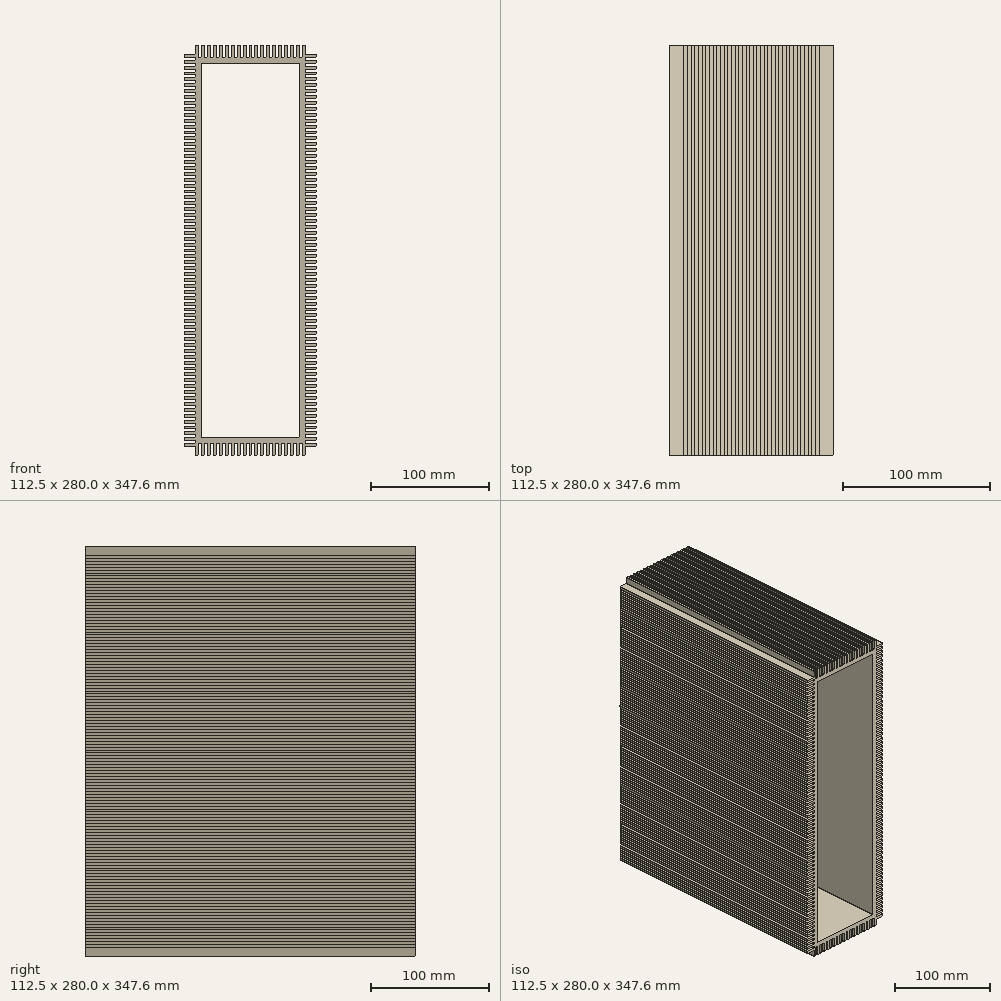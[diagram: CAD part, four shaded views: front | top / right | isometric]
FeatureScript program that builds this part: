
annotation { "Feature Type Name" : "Feature", "Feature Type Description" : "" }
export const myFeature = defineFeature(function(context is Context, id is Id, definition is map)
    precondition{}
    {
        {
            var Q0;
            Q0=qCreatedBy(makeId("Front.planeOp"),FACE);
            var sketch = newSketch(context, id + "F0", { "sketchPlane" : qUnion([Q0])});
            skLineSegment(sketch, "E0.bottom", {"start": v(40.56, -80) * mm, "end": v(-40.56, -80) * mm});
            skLineSegment(sketch, "E0.top", {"start": v(40.56, 80) * mm, "end": v(-40.56, 80) * mm});
            skLineSegment(sketch, "E0.left", {"start": v(40.56, -80) * mm, "end": v(40.56, 80) * mm});
            skLineSegment(sketch, "E0.right", {"start": v(-40.56, -80) * mm, "end": v(-40.56, 80) * mm});
            skPoint(sketch, "E0.middle", {"position": v(0, 0) * mm});
            skLineSegment(sketch, "E1", {"start": v(40.56, 80) * mm, "end": v(40.56, 85) * mm});
            skLineSegment(sketch, "E2", {"start": v(40.56, 85) * mm, "end": v(45.56, 85) * mm});
            skLineSegment(sketch, "E3.bottom", {"start": v(45.56, 85) * mm, "end": v(-45.56, 85) * mm});
            skLineSegment(sketch, "E3.left", {"start": v(45.56, 85) * mm, "end": v(45.56, -80) * mm});
            skLineSegment(sketch, "E3.right", {"start": v(-45.56, 85) * mm, "end": v(-45.56, -80) * mm});
            skLineSegment(sketch, "E4", {"start": v(-45.56, -80) * mm, "end": v(45.56, -80) * mm});
            skSolve(sketch);
        }
        {
            var Q0;
            Q0=makeQuery(id+"F0.imprint","IMPRINT",FACE,{"disambiguationData":[TD([[makeQuery(id+"F0.imprint","IMPRINT",EDGE,{"derivedFrom":sQuery(id+"F0.wireOp",EDGE,"E0.top")}),-1.0]])]});
            var Q1;
            {var subQ3=sQuery(id+"F0.wireOp",EDGE,"E0.left");Q1=makeQuery(id+"F0.imprint","IMPRINT",FACE,{"disambiguationData":[TD([[makeQuery(id+"F0.imprint","IMPRINT",EDGE,{"derivedFrom":subQ3}),-1.0]])]});}
            extrude(context, id + "F1", {"entities" : qUnion([Q0, Q1]), "depth" : 280 * mm, "offsetDistance" : 25 * mm});
        }
        {
            var Q0;
            Q0=makeQuery(id+"F1.opExtrude","SWEPT_FACE",FACE,{"disambiguationData":[OSD([sQuery(id+"F0.wireOp",EDGE,"E3.bottom")])]});
            extrude(context, id + "F2", {"entities" : qUnion([Q0]), "operationType" : NewBodyOperationType.ADD, "depth" : 0.05 * mm, "offsetDistance" : 25 * mm});
        }
        {
            var Q0;
            Q0=makeQuery(id+"F1.opExtrude","SWEPT_FACE",FACE,{"disambiguationData":[OSD([sQuery(id+"F0.wireOp",EDGE,"E0.top")])]});
            extrude(context, id + "F3", {"entities" : qUnion([Q0]), "operationType" : NewBodyOperationType.REMOVE, "oppositeDirection" : true, "depth" : 0.05 * mm, "offsetDistance" : 25 * mm});
        }
        {
            var Q0;
            {var subQ0=sQuery(id+"F0.wireOp",EDGE,"E3.left");Q0=makeQuery(id+"F2.boolean.opBoolean","MERGE",FACE,{"derivedFrom":[makeQuery(id+"F1.opExtrude","SWEPT_FACE",FACE,{"disambiguationData":[OSD([subQ0])]}),makeQuery(id+"F2.opExtrude","SWEPT_FACE",FACE,{"disambiguationData":[OSD([sQuery(id+"F0.wireOp",EDGE,"E3.bottom"),subQ0])]})]});}
            extrude(context, id + "F4", {"entities" : qUnion([Q0]), "operationType" : NewBodyOperationType.ADD, "depth" : 1.38 * mm, "offsetDistance" : 25 * mm});
        }
        {
            var Q0;
            {var subQ0=sQuery(id+"F0.wireOp",EDGE,"E0.left");Q0=makeQuery(id+"F3.boolean.opBoolean","MERGE",FACE,{"derivedFrom":[makeQuery(id+"F1.opExtrude","SWEPT_FACE",FACE,{"disambiguationData":[OSD([subQ0])]}),makeQuery(id+"F3.opExtrude","SWEPT_FACE",FACE,{"disambiguationData":[OSD([sQuery(id+"F0.wireOp",EDGE,"E0.top"),subQ0,sQuery(id+"F0.wireOp",EDGE,"E1")])]})]});}
            extrude(context, id + "F5", {"entities" : qUnion([Q0]), "operationType" : NewBodyOperationType.REMOVE, "oppositeDirection" : true, "depth" : 1.38 * mm, "offsetDistance" : 25 * mm});
        }
        {
            var Q0;
            Q0=makeQuery(id+"F1.opExtrude","CAP_FACE",FACE,{"disambiguationData":[OSD([sQuery(id+"F0.wireOp",EDGE,"E0.top"),sQuery(id+"F0.wireOp",EDGE,"E0.left"),sQuery(id+"F0.wireOp",EDGE,"E0.right"),sQuery(id+"F0.wireOp",EDGE,"E3.bottom"),sQuery(id+"F0.wireOp",EDGE,"E3.left"),sQuery(id+"F0.wireOp",EDGE,"E3.right"),sQuery(id+"F0.wireOp",EDGE,"E4")])],"isStart":false});
            var sketch = newSketch(context, id + "F6", { "sketchPlane" : qUnion([Q0])});
            skLineSegment(sketch, "E5.bottom", {"start": v(-45.56, -80) * mm, "end": v(-55.56, -80) * mm});
            skLineSegment(sketch, "E5.top", {"start": v(-45.56, -77.5) * mm, "end": v(-55.56, -77.5) * mm});
            skLineSegment(sketch, "E5.left", {"start": v(-45.56, -80) * mm, "end": v(-45.56, -77.5) * mm});
            skLineSegment(sketch, "E5.right", {"start": v(-55.56, -80) * mm, "end": v(-55.56, -77.5) * mm});
            skLineSegment(sketch, "E6", {"start": v(-45.56, -77.5) * mm, "end": v(-45.56, -75) * mm});
            skLineSegment(sketch, "E7.bottom", {"start": v(-45.56, -75) * mm, "end": v(-55.56, -75) * mm});
            skLineSegment(sketch, "E7.top", {"start": v(-45.56, -72.5) * mm, "end": v(-55.56, -72.5) * mm});
            skLineSegment(sketch, "E7.left", {"start": v(-45.56, -75) * mm, "end": v(-45.56, -72.5) * mm});
            skLineSegment(sketch, "E7.right", {"start": v(-55.56, -75) * mm, "end": v(-55.56, -72.5) * mm});
            skLineSegment(sketch, "E8", {"start": v(-45.56, -72.5) * mm, "end": v(-45.56, -70) * mm});
            skLineSegment(sketch, "E9.bottom", {"start": v(-45.56, -70) * mm, "end": v(-55.56, -70) * mm});
            skLineSegment(sketch, "E9.top", {"start": v(-45.56, -67.5) * mm, "end": v(-55.56, -67.5) * mm});
            skLineSegment(sketch, "E9.left", {"start": v(-45.56, -70) * mm, "end": v(-45.56, -67.5) * mm});
            skLineSegment(sketch, "E9.right", {"start": v(-55.56, -70) * mm, "end": v(-55.56, -67.5) * mm});
            skLineSegment(sketch, "E10", {"start": v(-45.56, -67.5) * mm, "end": v(-45.56, -65) * mm});
            skLineSegment(sketch, "E11.bottom", {"start": v(-45.56, -65) * mm, "end": v(-55.56, -65) * mm});
            skLineSegment(sketch, "E11.top", {"start": v(-45.56, -62.5) * mm, "end": v(-55.56, -62.5) * mm});
            skLineSegment(sketch, "E11.left", {"start": v(-45.56, -65) * mm, "end": v(-45.56, -62.5) * mm});
            skLineSegment(sketch, "E11.right", {"start": v(-55.56, -65) * mm, "end": v(-55.56, -62.5) * mm});
            skLineSegment(sketch, "E12", {"start": v(-45.56, -62.5) * mm, "end": v(-45.56, -60) * mm});
            skLineSegment(sketch, "E13.bottom", {"start": v(-45.56, -60) * mm, "end": v(-55.56, -60) * mm});
            skLineSegment(sketch, "E13.top", {"start": v(-45.56, -57.5) * mm, "end": v(-55.56, -57.5) * mm});
            skLineSegment(sketch, "E13.left", {"start": v(-45.56, -60) * mm, "end": v(-45.56, -57.5) * mm});
            skLineSegment(sketch, "E13.right", {"start": v(-55.56, -60) * mm, "end": v(-55.56, -57.5) * mm});
            skLineSegment(sketch, "E14", {"start": v(-45.56, -57.5) * mm, "end": v(-45.56, -55) * mm});
            skLineSegment(sketch, "E15.bottom", {"start": v(-45.56, -55) * mm, "end": v(-55.56, -55) * mm});
            skLineSegment(sketch, "E15.top", {"start": v(-45.56, -52.5) * mm, "end": v(-55.56, -52.5) * mm});
            skLineSegment(sketch, "E15.left", {"start": v(-45.56, -55) * mm, "end": v(-45.56, -52.5) * mm});
            skLineSegment(sketch, "E15.right", {"start": v(-55.56, -55) * mm, "end": v(-55.56, -52.5) * mm});
            skLineSegment(sketch, "E16", {"start": v(-45.56, -52.5) * mm, "end": v(-45.56, -50) * mm});
            skLineSegment(sketch, "E17.bottom", {"start": v(-45.56, -50) * mm, "end": v(-55.56, -50) * mm});
            skLineSegment(sketch, "E17.top", {"start": v(-45.56, -47.5) * mm, "end": v(-55.56, -47.5) * mm});
            skLineSegment(sketch, "E17.left", {"start": v(-45.56, -50) * mm, "end": v(-45.56, -47.5) * mm});
            skLineSegment(sketch, "E17.right", {"start": v(-55.56, -50) * mm, "end": v(-55.56, -47.5) * mm});
            skLineSegment(sketch, "E18", {"start": v(-45.56, -47.5) * mm, "end": v(-45.56, -45) * mm});
            skLineSegment(sketch, "E19.bottom", {"start": v(-45.56, -45) * mm, "end": v(-55.56, -45) * mm});
            skLineSegment(sketch, "E19.top", {"start": v(-45.56, -42.5) * mm, "end": v(-55.56, -42.5) * mm});
            skLineSegment(sketch, "E19.left", {"start": v(-45.56, -45) * mm, "end": v(-45.56, -42.5) * mm});
            skLineSegment(sketch, "E19.right", {"start": v(-55.56, -45) * mm, "end": v(-55.56, -42.5) * mm});
            skLineSegment(sketch, "E20", {"start": v(-45.56, -42.5) * mm, "end": v(-45.56, -40) * mm});
            skLineSegment(sketch, "E21.bottom", {"start": v(-45.56, -40) * mm, "end": v(-55.56, -40) * mm});
            skLineSegment(sketch, "E21.top", {"start": v(-45.56, -37.5) * mm, "end": v(-55.56, -37.5) * mm});
            skLineSegment(sketch, "E21.left", {"start": v(-45.56, -40) * mm, "end": v(-45.56, -37.5) * mm});
            skLineSegment(sketch, "E21.right", {"start": v(-55.56, -40) * mm, "end": v(-55.56, -37.5) * mm});
            skLineSegment(sketch, "E22", {"start": v(-45.56, -37.5) * mm, "end": v(-45.56, -35) * mm});
            skLineSegment(sketch, "E23.bottom", {"start": v(-45.56, -35) * mm, "end": v(-55.56, -35) * mm});
            skLineSegment(sketch, "E23.top", {"start": v(-45.56, -32.5) * mm, "end": v(-55.56, -32.5) * mm});
            skLineSegment(sketch, "E23.left", {"start": v(-45.56, -35) * mm, "end": v(-45.56, -32.5) * mm});
            skLineSegment(sketch, "E23.right", {"start": v(-55.56, -35) * mm, "end": v(-55.56, -32.5) * mm});
            skLineSegment(sketch, "E24", {"start": v(-45.56, -32.5) * mm, "end": v(-45.56, -30) * mm});
            skLineSegment(sketch, "E25.bottom", {"start": v(-45.56, -30) * mm, "end": v(-55.56, -30) * mm});
            skLineSegment(sketch, "E25.top", {"start": v(-45.56, -27.5) * mm, "end": v(-55.56, -27.5) * mm});
            skLineSegment(sketch, "E25.left", {"start": v(-45.56, -30) * mm, "end": v(-45.56, -27.5) * mm});
            skLineSegment(sketch, "E25.right", {"start": v(-55.56, -30) * mm, "end": v(-55.56, -27.5) * mm});
            skLineSegment(sketch, "E26", {"start": v(-45.56, -27.5) * mm, "end": v(-45.56, -25) * mm});
            skLineSegment(sketch, "E27.bottom", {"start": v(-45.56, -25) * mm, "end": v(-55.56, -25) * mm});
            skLineSegment(sketch, "E27.top", {"start": v(-45.56, -22.5) * mm, "end": v(-55.56, -22.5) * mm});
            skLineSegment(sketch, "E27.left", {"start": v(-45.56, -25) * mm, "end": v(-45.56, -22.5) * mm});
            skLineSegment(sketch, "E27.right", {"start": v(-55.56, -25) * mm, "end": v(-55.56, -22.5) * mm});
            skLineSegment(sketch, "E28", {"start": v(-45.56, -22.5) * mm, "end": v(-45.56, -20) * mm});
            skLineSegment(sketch, "E29.bottom", {"start": v(-45.56, -20) * mm, "end": v(-55.56, -20) * mm});
            skLineSegment(sketch, "E29.top", {"start": v(-45.56, -17.5) * mm, "end": v(-55.56, -17.5) * mm});
            skLineSegment(sketch, "E29.left", {"start": v(-45.56, -20) * mm, "end": v(-45.56, -17.5) * mm});
            skLineSegment(sketch, "E29.right", {"start": v(-55.56, -20) * mm, "end": v(-55.56, -17.5) * mm});
            skLineSegment(sketch, "E30", {"start": v(-45.56, -17.5) * mm, "end": v(-45.56, -15) * mm});
            skLineSegment(sketch, "E31.bottom", {"start": v(-45.56, -15) * mm, "end": v(-55.56, -15) * mm});
            skLineSegment(sketch, "E31.top", {"start": v(-45.56, -12.5) * mm, "end": v(-55.56, -12.5) * mm});
            skLineSegment(sketch, "E31.left", {"start": v(-45.56, -15) * mm, "end": v(-45.56, -12.5) * mm});
            skLineSegment(sketch, "E31.right", {"start": v(-55.56, -15) * mm, "end": v(-55.56, -12.5) * mm});
            skLineSegment(sketch, "E32", {"start": v(-45.56, -12.5) * mm, "end": v(-45.56, -10) * mm});
            skLineSegment(sketch, "E33.bottom", {"start": v(-45.56, -10) * mm, "end": v(-55.56, -10) * mm});
            skLineSegment(sketch, "E33.top", {"start": v(-45.56, -7.5) * mm, "end": v(-55.56, -7.5) * mm});
            skLineSegment(sketch, "E33.left", {"start": v(-45.56, -10) * mm, "end": v(-45.56, -7.5) * mm});
            skLineSegment(sketch, "E33.right", {"start": v(-55.56, -10) * mm, "end": v(-55.56, -7.5) * mm});
            skLineSegment(sketch, "E34", {"start": v(-45.56, -7.5) * mm, "end": v(-45.56, -5) * mm});
            skLineSegment(sketch, "E35.bottom", {"start": v(-45.56, -5) * mm, "end": v(-55.56, -5) * mm});
            skLineSegment(sketch, "E35.top", {"start": v(-45.56, -2.5) * mm, "end": v(-55.56, -2.5) * mm});
            skLineSegment(sketch, "E35.left", {"start": v(-45.56, -5) * mm, "end": v(-45.56, -2.5) * mm});
            skLineSegment(sketch, "E35.right", {"start": v(-55.56, -5) * mm, "end": v(-55.56, -2.5) * mm});
            skLineSegment(sketch, "E36", {"start": v(-45.56, -2.5) * mm, "end": v(-45.56, 0) * mm});
            skLineSegment(sketch, "E37.bottom", {"start": v(-45.56, 0.05) * mm, "end": v(-55.56, 0.05) * mm});
            skLineSegment(sketch, "E37.top", {"start": v(-45.56, 2.55) * mm, "end": v(-55.56, 2.55) * mm});
            skLineSegment(sketch, "E37.left", {"start": v(-45.56, 0.05) * mm, "end": v(-45.56, 2.55) * mm});
            skLineSegment(sketch, "E37.right", {"start": v(-55.56, 0.05) * mm, "end": v(-55.56, 2.55) * mm});
            skLineSegment(sketch, "E38", {"start": v(-45.56, 2.55) * mm, "end": v(-45.56, 5.05) * mm});
            skLineSegment(sketch, "E39.bottom", {"start": v(-45.56, 5.05) * mm, "end": v(-55.56, 5.05) * mm});
            skLineSegment(sketch, "E39.top", {"start": v(-45.56, 7.55) * mm, "end": v(-55.56, 7.55) * mm});
            skLineSegment(sketch, "E39.left", {"start": v(-45.56, 5.05) * mm, "end": v(-45.56, 7.55) * mm});
            skLineSegment(sketch, "E39.right", {"start": v(-55.56, 5.05) * mm, "end": v(-55.56, 7.55) * mm});
            skLineSegment(sketch, "E40", {"start": v(-45.56, 7.55) * mm, "end": v(-45.56, 10.05) * mm});
            skLineSegment(sketch, "E41.bottom", {"start": v(-45.56, 10.05) * mm, "end": v(-55.56, 10.05) * mm});
            skLineSegment(sketch, "E41.top", {"start": v(-45.56, 12.55) * mm, "end": v(-55.56, 12.55) * mm});
            skLineSegment(sketch, "E41.left", {"start": v(-45.56, 10.05) * mm, "end": v(-45.56, 12.55) * mm});
            skLineSegment(sketch, "E41.right", {"start": v(-55.56, 10.05) * mm, "end": v(-55.56, 12.55) * mm});
            skLineSegment(sketch, "E42", {"start": v(-45.56, 12.55) * mm, "end": v(-45.56, 15.05) * mm});
            skLineSegment(sketch, "E43.bottom", {"start": v(-45.56, 15.05) * mm, "end": v(-55.56, 15.05) * mm});
            skLineSegment(sketch, "E43.top", {"start": v(-45.56, 17.55) * mm, "end": v(-55.56, 17.55) * mm});
            skLineSegment(sketch, "E43.left", {"start": v(-45.56, 15.05) * mm, "end": v(-45.56, 17.55) * mm});
            skLineSegment(sketch, "E43.right", {"start": v(-55.56, 15.05) * mm, "end": v(-55.56, 17.55) * mm});
            skLineSegment(sketch, "E44", {"start": v(-45.56, 17.55) * mm, "end": v(-45.56, 20.05) * mm});
            skLineSegment(sketch, "E45.bottom", {"start": v(-45.56, 20.05) * mm, "end": v(-55.56, 20.05) * mm});
            skLineSegment(sketch, "E45.top", {"start": v(-45.56, 22.55) * mm, "end": v(-55.56, 22.55) * mm});
            skLineSegment(sketch, "E45.left", {"start": v(-45.56, 20.05) * mm, "end": v(-45.56, 22.55) * mm});
            skLineSegment(sketch, "E45.right", {"start": v(-55.56, 20.05) * mm, "end": v(-55.56, 22.55) * mm});
            skLineSegment(sketch, "E46", {"start": v(-45.56, 22.55) * mm, "end": v(-45.56, 25.05) * mm});
            skLineSegment(sketch, "E47.bottom", {"start": v(-45.56, 25.05) * mm, "end": v(-55.56, 25.05) * mm});
            skLineSegment(sketch, "E47.top", {"start": v(-45.56, 27.55) * mm, "end": v(-55.56, 27.55) * mm});
            skLineSegment(sketch, "E47.left", {"start": v(-45.56, 25.05) * mm, "end": v(-45.56, 27.55) * mm});
            skLineSegment(sketch, "E47.right", {"start": v(-55.56, 25.05) * mm, "end": v(-55.56, 27.55) * mm});
            skLineSegment(sketch, "E48", {"start": v(-45.56, 27.55) * mm, "end": v(-45.56, 30.05) * mm});
            skLineSegment(sketch, "E49.bottom", {"start": v(-45.56, 30.05) * mm, "end": v(-55.56, 30.05) * mm});
            skLineSegment(sketch, "E49.top", {"start": v(-45.56, 32.55) * mm, "end": v(-55.56, 32.55) * mm});
            skLineSegment(sketch, "E49.left", {"start": v(-45.56, 30.05) * mm, "end": v(-45.56, 32.55) * mm});
            skLineSegment(sketch, "E49.right", {"start": v(-55.56, 30.05) * mm, "end": v(-55.56, 32.55) * mm});
            skLineSegment(sketch, "E50", {"start": v(-45.56, 32.55) * mm, "end": v(-45.56, 35.05) * mm});
            skLineSegment(sketch, "E51.bottom", {"start": v(-45.56, 35.05) * mm, "end": v(-55.56, 35.05) * mm});
            skLineSegment(sketch, "E51.top", {"start": v(-45.56, 37.55) * mm, "end": v(-55.56, 37.55) * mm});
            skLineSegment(sketch, "E51.left", {"start": v(-45.56, 35.05) * mm, "end": v(-45.56, 37.55) * mm});
            skLineSegment(sketch, "E51.right", {"start": v(-55.56, 35.05) * mm, "end": v(-55.56, 37.55) * mm});
            skLineSegment(sketch, "E52", {"start": v(-45.56, 37.55) * mm, "end": v(-45.56, 40.05) * mm});
            skLineSegment(sketch, "E53.bottom", {"start": v(-45.56, 40.05) * mm, "end": v(-55.56, 40.05) * mm});
            skLineSegment(sketch, "E53.top", {"start": v(-45.56, 42.55) * mm, "end": v(-55.56, 42.55) * mm});
            skLineSegment(sketch, "E53.left", {"start": v(-45.56, 40.05) * mm, "end": v(-45.56, 42.55) * mm});
            skLineSegment(sketch, "E53.right", {"start": v(-55.56, 40.05) * mm, "end": v(-55.56, 42.55) * mm});
            skLineSegment(sketch, "E54", {"start": v(-45.56, 42.55) * mm, "end": v(-45.56, 45.05) * mm});
            skLineSegment(sketch, "E55.bottom", {"start": v(-45.56, 45.05) * mm, "end": v(-55.56, 45.05) * mm});
            skLineSegment(sketch, "E55.top", {"start": v(-45.56, 47.55) * mm, "end": v(-55.56, 47.55) * mm});
            skLineSegment(sketch, "E55.left", {"start": v(-45.56, 45.05) * mm, "end": v(-45.56, 47.55) * mm});
            skLineSegment(sketch, "E55.right", {"start": v(-55.56, 45.05) * mm, "end": v(-55.56, 47.55) * mm});
            skLineSegment(sketch, "E56", {"start": v(-45.56, 47.55) * mm, "end": v(-45.56, 50.05) * mm});
            skLineSegment(sketch, "E57.bottom", {"start": v(-45.56, 50.05) * mm, "end": v(-55.56, 50.05) * mm});
            skLineSegment(sketch, "E57.top", {"start": v(-45.56, 52.55) * mm, "end": v(-55.56, 52.55) * mm});
            skLineSegment(sketch, "E57.left", {"start": v(-45.56, 50.05) * mm, "end": v(-45.56, 52.55) * mm});
            skLineSegment(sketch, "E57.right", {"start": v(-55.56, 50.05) * mm, "end": v(-55.56, 52.55) * mm});
            skLineSegment(sketch, "E58", {"start": v(-45.56, 52.55) * mm, "end": v(-45.56, 55.05) * mm});
            skLineSegment(sketch, "E59.bottom", {"start": v(-45.56, 55.05) * mm, "end": v(-55.56, 55.05) * mm});
            skLineSegment(sketch, "E59.top", {"start": v(-45.56, 57.55) * mm, "end": v(-55.56, 57.55) * mm});
            skLineSegment(sketch, "E59.left", {"start": v(-45.56, 55.05) * mm, "end": v(-45.56, 57.55) * mm});
            skLineSegment(sketch, "E59.right", {"start": v(-55.56, 55.05) * mm, "end": v(-55.56, 57.55) * mm});
            skLineSegment(sketch, "E60", {"start": v(-45.56, 57.55) * mm, "end": v(-45.56, 60.05) * mm});
            skLineSegment(sketch, "E61.bottom", {"start": v(-45.56, 60.05) * mm, "end": v(-55.56, 60.05) * mm});
            skLineSegment(sketch, "E61.top", {"start": v(-45.56, 62.55) * mm, "end": v(-55.56, 62.55) * mm});
            skLineSegment(sketch, "E61.left", {"start": v(-45.56, 60.05) * mm, "end": v(-45.56, 62.55) * mm});
            skLineSegment(sketch, "E61.right", {"start": v(-55.56, 60.05) * mm, "end": v(-55.56, 62.55) * mm});
            skLineSegment(sketch, "E62", {"start": v(-45.56, 62.55) * mm, "end": v(-45.56, 65.05) * mm});
            skLineSegment(sketch, "E63.bottom", {"start": v(-45.56, 65.05) * mm, "end": v(-55.56, 65.05) * mm});
            skLineSegment(sketch, "E63.top", {"start": v(-45.56, 67.55) * mm, "end": v(-55.56, 67.55) * mm});
            skLineSegment(sketch, "E63.left", {"start": v(-45.56, 65.05) * mm, "end": v(-45.56, 67.55) * mm});
            skLineSegment(sketch, "E63.right", {"start": v(-55.56, 65.05) * mm, "end": v(-55.56, 67.55) * mm});
            skLineSegment(sketch, "E64", {"start": v(-45.56, 67.55) * mm, "end": v(-45.56, 70.05) * mm});
            skLineSegment(sketch, "E65.bottom", {"start": v(-45.56, 70.05) * mm, "end": v(-55.56, 70.05) * mm});
            skLineSegment(sketch, "E65.top", {"start": v(-45.56, 72.55) * mm, "end": v(-55.56, 72.55) * mm});
            skLineSegment(sketch, "E65.left", {"start": v(-45.56, 70.05) * mm, "end": v(-45.56, 72.55) * mm});
            skLineSegment(sketch, "E65.right", {"start": v(-55.56, 70.05) * mm, "end": v(-55.56, 72.55) * mm});
            skLineSegment(sketch, "E66", {"start": v(-45.56, 72.55) * mm, "end": v(-45.56, 75.05) * mm});
            skLineSegment(sketch, "E67.bottom", {"start": v(-45.56, 75.05) * mm, "end": v(-55.56, 75.05) * mm});
            skLineSegment(sketch, "E67.top", {"start": v(-45.56, 77.55) * mm, "end": v(-55.56, 77.55) * mm});
            skLineSegment(sketch, "E67.left", {"start": v(-45.56, 75.05) * mm, "end": v(-45.56, 77.55) * mm});
            skLineSegment(sketch, "E67.right", {"start": v(-55.56, 75.05) * mm, "end": v(-55.56, 77.55) * mm});
            skLineSegment(sketch, "E68", {"start": v(-45.56, 77.55) * mm, "end": v(-45.56, 80.05) * mm});
            skLineSegment(sketch, "E69.bottom", {"start": v(-45.56, 80.05) * mm, "end": v(-55.56, 80.05) * mm});
            skLineSegment(sketch, "E69.top", {"start": v(-45.56, 82.55) * mm, "end": v(-55.56, 82.55) * mm});
            skLineSegment(sketch, "E69.left", {"start": v(-45.56, 80.05) * mm, "end": v(-45.56, 82.55) * mm});
            skLineSegment(sketch, "E69.right", {"start": v(-55.56, 80.05) * mm, "end": v(-55.56, 82.55) * mm});
            skLineSegment(sketch, "E70", {"start": v(-45.56, 82.55) * mm, "end": v(-45.56, 85.05) * mm});
            skLineSegment(sketch, "E71.bottom", {"start": v(-45.56, 85.05) * mm, "end": v(-55.56, 85.05) * mm});
            skLineSegment(sketch, "E71.top", {"start": v(-45.56, 87.55) * mm, "end": v(-55.56, 87.55) * mm});
            skLineSegment(sketch, "E71.left", {"start": v(-45.56, 85.05) * mm, "end": v(-45.56, 87.55) * mm});
            skLineSegment(sketch, "E71.right", {"start": v(-55.56, 85.05) * mm, "end": v(-55.56, 87.55) * mm});
            skLineSegment(sketch, "E72.bottom", {"start": v(-45.56, 85.05) * mm, "end": v(-43.06, 85.05) * mm});
            skLineSegment(sketch, "E72.top", {"start": v(-45.56, 95.05) * mm, "end": v(-43.06, 95.05) * mm});
            skLineSegment(sketch, "E72.left", {"start": v(-45.56, 85.05) * mm, "end": v(-45.56, 95.05) * mm});
            skLineSegment(sketch, "E72.right", {"start": v(-43.06, 85.05) * mm, "end": v(-43.06, 95.05) * mm});
            skLineSegment(sketch, "E73", {"start": v(-43.06, 85.05) * mm, "end": v(-40.56, 85.05) * mm});
            skLineSegment(sketch, "E74.bottom", {"start": v(-40.56, 85.05) * mm, "end": v(-38.06, 85.05) * mm});
            skLineSegment(sketch, "E74.top", {"start": v(-40.56, 95.05) * mm, "end": v(-38.06, 95.05) * mm});
            skLineSegment(sketch, "E74.left", {"start": v(-40.56, 85.05) * mm, "end": v(-40.56, 95.05) * mm});
            skLineSegment(sketch, "E74.right", {"start": v(-38.06, 85.05) * mm, "end": v(-38.06, 95.05) * mm});
            skLineSegment(sketch, "E75", {"start": v(-38.06, 85.05) * mm, "end": v(-35.56, 85.05) * mm});
            skLineSegment(sketch, "E76.bottom", {"start": v(-35.56, 85.05) * mm, "end": v(-33.06, 85.05) * mm});
            skLineSegment(sketch, "E76.top", {"start": v(-35.56, 95.05) * mm, "end": v(-33.06, 95.05) * mm});
            skLineSegment(sketch, "E76.left", {"start": v(-35.56, 85.05) * mm, "end": v(-35.56, 95.05) * mm});
            skLineSegment(sketch, "E76.right", {"start": v(-33.06, 85.05) * mm, "end": v(-33.06, 95.05) * mm});
            skLineSegment(sketch, "E77", {"start": v(-33.06, 85.05) * mm, "end": v(-30.56, 85.05) * mm});
            skLineSegment(sketch, "E78.bottom", {"start": v(-30.56, 85.05) * mm, "end": v(-28.06, 85.05) * mm});
            skLineSegment(sketch, "E78.top", {"start": v(-30.56, 95.05) * mm, "end": v(-28.06, 95.05) * mm});
            skLineSegment(sketch, "E78.left", {"start": v(-30.56, 85.05) * mm, "end": v(-30.56, 95.05) * mm});
            skLineSegment(sketch, "E78.right", {"start": v(-28.06, 85.05) * mm, "end": v(-28.06, 95.05) * mm});
            skLineSegment(sketch, "E79", {"start": v(-28.06, 85.05) * mm, "end": v(-25.56, 85.05) * mm});
            skLineSegment(sketch, "E80.bottom", {"start": v(-25.56, 85.05) * mm, "end": v(-23.06, 85.05) * mm});
            skLineSegment(sketch, "E80.top", {"start": v(-25.56, 95.05) * mm, "end": v(-23.06, 95.05) * mm});
            skLineSegment(sketch, "E80.left", {"start": v(-25.56, 85.05) * mm, "end": v(-25.56, 95.05) * mm});
            skLineSegment(sketch, "E80.right", {"start": v(-23.06, 85.05) * mm, "end": v(-23.06, 95.05) * mm});
            skLineSegment(sketch, "E81", {"start": v(-23.06, 85.05) * mm, "end": v(-20.56, 85.05) * mm});
            skLineSegment(sketch, "E82.bottom", {"start": v(-20.56, 85.05) * mm, "end": v(-18.06, 85.05) * mm});
            skLineSegment(sketch, "E82.top", {"start": v(-20.56, 95.05) * mm, "end": v(-18.06, 95.05) * mm});
            skLineSegment(sketch, "E82.left", {"start": v(-20.56, 85.05) * mm, "end": v(-20.56, 95.05) * mm});
            skLineSegment(sketch, "E82.right", {"start": v(-18.06, 85.05) * mm, "end": v(-18.06, 95.05) * mm});
            skLineSegment(sketch, "E83", {"start": v(-18.06, 85.05) * mm, "end": v(-15.56, 85.05) * mm});
            skLineSegment(sketch, "E84.bottom", {"start": v(-15.56, 85.05) * mm, "end": v(-13.06, 85.05) * mm});
            skLineSegment(sketch, "E84.top", {"start": v(-15.56, 95.05) * mm, "end": v(-13.06, 95.05) * mm});
            skLineSegment(sketch, "E84.left", {"start": v(-15.56, 85.05) * mm, "end": v(-15.56, 95.05) * mm});
            skLineSegment(sketch, "E84.right", {"start": v(-13.06, 85.05) * mm, "end": v(-13.06, 95.05) * mm});
            skLineSegment(sketch, "E85", {"start": v(-13.06, 85.05) * mm, "end": v(-10.56, 85.05) * mm});
            skLineSegment(sketch, "E86.bottom", {"start": v(-10.56, 85.05) * mm, "end": v(-8.06, 85.05) * mm});
            skLineSegment(sketch, "E86.top", {"start": v(-10.56, 95.05) * mm, "end": v(-8.06, 95.05) * mm});
            skLineSegment(sketch, "E86.left", {"start": v(-10.56, 85.05) * mm, "end": v(-10.56, 95.05) * mm});
            skLineSegment(sketch, "E86.right", {"start": v(-8.06, 85.05) * mm, "end": v(-8.06, 95.05) * mm});
            skLineSegment(sketch, "E87", {"start": v(-8.06, 85.05) * mm, "end": v(-5.56, 85.05) * mm});
            skLineSegment(sketch, "E88.bottom", {"start": v(-5.56, 85.05) * mm, "end": v(-3.06, 85.05) * mm});
            skLineSegment(sketch, "E88.top", {"start": v(-5.56, 95.05) * mm, "end": v(-3.06, 95.05) * mm});
            skLineSegment(sketch, "E88.left", {"start": v(-5.56, 85.05) * mm, "end": v(-5.56, 95.05) * mm});
            skLineSegment(sketch, "E88.right", {"start": v(-3.06, 85.05) * mm, "end": v(-3.06, 95.05) * mm});
            skLineSegment(sketch, "E89", {"start": v(-3.06, 85.05) * mm, "end": v(-0.56, 85.05) * mm});
            skLineSegment(sketch, "E90.bottom", {"start": v(-0.56, 85.05) * mm, "end": v(1.94, 85.05) * mm});
            skLineSegment(sketch, "E90.top", {"start": v(-0.56, 95.05) * mm, "end": v(1.94, 95.05) * mm});
            skLineSegment(sketch, "E90.left", {"start": v(-0.56, 85.05) * mm, "end": v(-0.56, 95.05) * mm});
            skLineSegment(sketch, "E90.right", {"start": v(1.94, 85.05) * mm, "end": v(1.94, 95.05) * mm});
            skLineSegment(sketch, "E91.bottom", {"start": v(1.94, 85.05) * mm, "end": v(4.44, 85.05) * mm});
            skLineSegment(sketch, "E91.top", {"start": v(1.94, 85.05) * mm, "end": v(4.44, 85.05) * mm});
            skLineSegment(sketch, "E91.left", {"start": v(1.94, 85.05) * mm, "end": v(1.94, 85.05) * mm});
            skLineSegment(sketch, "E91.right", {"start": v(4.44, 85.05) * mm, "end": v(4.44, 85.05) * mm});
            skLineSegment(sketch, "E92.bottom", {"start": v(4.44, 85.05) * mm, "end": v(6.94, 85.05) * mm});
            skLineSegment(sketch, "E92.top", {"start": v(4.44, 95.05) * mm, "end": v(6.94, 95.05) * mm});
            skLineSegment(sketch, "E92.left", {"start": v(4.44, 85.05) * mm, "end": v(4.44, 95.05) * mm});
            skLineSegment(sketch, "E92.right", {"start": v(6.94, 85.05) * mm, "end": v(6.94, 95.05) * mm});
            skLineSegment(sketch, "E93", {"start": v(6.94, 85.05) * mm, "end": v(9.44, 85.05) * mm});
            skLineSegment(sketch, "E94.bottom", {"start": v(9.44, 85.05) * mm, "end": v(11.94, 85.05) * mm});
            skLineSegment(sketch, "E94.top", {"start": v(9.44, 95.05) * mm, "end": v(11.94, 95.05) * mm});
            skLineSegment(sketch, "E94.left", {"start": v(9.44, 85.05) * mm, "end": v(9.44, 95.05) * mm});
            skLineSegment(sketch, "E94.right", {"start": v(11.94, 85.05) * mm, "end": v(11.94, 95.05) * mm});
            skLineSegment(sketch, "E95", {"start": v(11.94, 85.05) * mm, "end": v(14.44, 85.05) * mm});
            skLineSegment(sketch, "E96.bottom", {"start": v(14.44, 85.05) * mm, "end": v(16.94, 85.05) * mm});
            skLineSegment(sketch, "E96.top", {"start": v(14.44, 95.05) * mm, "end": v(16.94, 95.05) * mm});
            skLineSegment(sketch, "E96.left", {"start": v(14.44, 85.05) * mm, "end": v(14.44, 95.05) * mm});
            skLineSegment(sketch, "E96.right", {"start": v(16.94, 85.05) * mm, "end": v(16.94, 95.05) * mm});
            skLineSegment(sketch, "E97", {"start": v(16.94, 85.05) * mm, "end": v(19.44, 85.05) * mm});
            skLineSegment(sketch, "E98.bottom", {"start": v(19.44, 85.05) * mm, "end": v(21.94, 85.05) * mm});
            skLineSegment(sketch, "E98.top", {"start": v(19.44, 95.05) * mm, "end": v(21.94, 95.05) * mm});
            skLineSegment(sketch, "E98.left", {"start": v(19.44, 85.05) * mm, "end": v(19.44, 95.05) * mm});
            skLineSegment(sketch, "E98.right", {"start": v(21.94, 85.05) * mm, "end": v(21.94, 95.05) * mm});
            skLineSegment(sketch, "E99", {"start": v(21.94, 85.05) * mm, "end": v(24.44, 85.05) * mm});
            skLineSegment(sketch, "E100.bottom", {"start": v(24.44, 85.05) * mm, "end": v(26.94, 85.05) * mm});
            skLineSegment(sketch, "E100.top", {"start": v(24.44, 95.05) * mm, "end": v(26.94, 95.05) * mm});
            skLineSegment(sketch, "E100.left", {"start": v(24.44, 85.05) * mm, "end": v(24.44, 95.05) * mm});
            skLineSegment(sketch, "E100.right", {"start": v(26.94, 85.05) * mm, "end": v(26.94, 95.05) * mm});
            skLineSegment(sketch, "E101", {"start": v(26.94, 85.05) * mm, "end": v(29.44, 85.05) * mm});
            skLineSegment(sketch, "E102.bottom", {"start": v(29.44, 85.05) * mm, "end": v(31.94, 85.05) * mm});
            skLineSegment(sketch, "E102.top", {"start": v(29.44, 95.05) * mm, "end": v(31.94, 95.05) * mm});
            skLineSegment(sketch, "E102.left", {"start": v(29.44, 85.05) * mm, "end": v(29.44, 95.05) * mm});
            skLineSegment(sketch, "E102.right", {"start": v(31.94, 85.05) * mm, "end": v(31.94, 95.05) * mm});
            skLineSegment(sketch, "E103", {"start": v(31.94, 85.05) * mm, "end": v(34.44, 85.05) * mm});
            skLineSegment(sketch, "E104.bottom", {"start": v(34.44, 85.05) * mm, "end": v(36.94, 85.05) * mm});
            skLineSegment(sketch, "E104.top", {"start": v(34.44, 95.05) * mm, "end": v(36.94, 95.05) * mm});
            skLineSegment(sketch, "E104.left", {"start": v(34.44, 85.05) * mm, "end": v(34.44, 95.05) * mm});
            skLineSegment(sketch, "E104.right", {"start": v(36.94, 85.05) * mm, "end": v(36.94, 95.05) * mm});
            skLineSegment(sketch, "E105", {"start": v(36.94, 85.05) * mm, "end": v(39.44, 85.05) * mm});
            skLineSegment(sketch, "E106.bottom", {"start": v(39.44, 85.05) * mm, "end": v(41.94, 85.05) * mm});
            skLineSegment(sketch, "E106.top", {"start": v(39.44, 95.05) * mm, "end": v(41.94, 95.05) * mm});
            skLineSegment(sketch, "E106.left", {"start": v(39.44, 85.05) * mm, "end": v(39.44, 95.05) * mm});
            skLineSegment(sketch, "E106.right", {"start": v(41.94, 85.05) * mm, "end": v(41.94, 95.05) * mm});
            skLineSegment(sketch, "E107", {"start": v(41.94, 85.05) * mm, "end": v(44.44, 85.05) * mm});
            skLineSegment(sketch, "E108.top", {"start": v(44.44, 95.05) * mm, "end": v(46.94, 95.05) * mm});
            skLineSegment(sketch, "E108.left", {"start": v(44.44, 85.05) * mm, "end": v(44.44, 95.05) * mm});
            skLineSegment(sketch, "E109", {"start": v(46.94, 95.05) * mm, "end": v(46.94, 85.05) * mm});
            skLineSegment(sketch, "E110", {"start": v(46.94, 85.05) * mm, "end": v(44.44, 85.05) * mm});
            skLineSegment(sketch, "E111.MirrorCS", {"start": v(46.94, 25.05) * mm, "end": v(56.94, 25.05) * mm});
            skLineSegment(sketch, "E112.MirrorCS", {"start": v(46.94, 27.55) * mm, "end": v(56.94, 27.55) * mm});
            skLineSegment(sketch, "E113.MirrorCS", {"start": v(46.94, 22.55) * mm, "end": v(56.94, 22.55) * mm});
            skLineSegment(sketch, "E114.MirrorCS", {"start": v(46.94, 35.05) * mm, "end": v(56.94, 35.05) * mm});
            skLineSegment(sketch, "E115.MirrorCS", {"start": v(46.94, 42.55) * mm, "end": v(56.94, 42.55) * mm});
            skLineSegment(sketch, "E116.MirrorCS", {"start": v(46.94, -22.5) * mm, "end": v(56.94, -22.5) * mm});
            skLineSegment(sketch, "E117.MirrorCS", {"start": v(46.94, 32.55) * mm, "end": v(56.94, 32.55) * mm});
            skLineSegment(sketch, "E118.MirrorCS", {"start": v(46.94, 40.05) * mm, "end": v(56.94, 40.05) * mm});
            skLineSegment(sketch, "E119.MirrorCS", {"start": v(56.94, 25.05) * mm, "end": v(56.94, 27.55) * mm});
            skLineSegment(sketch, "E120.MirrorCS", {"start": v(46.94, 30.05) * mm, "end": v(56.94, 30.05) * mm});
            skLineSegment(sketch, "E121.MirrorCS", {"start": v(46.94, -25) * mm, "end": v(56.94, -25) * mm});
            skLineSegment(sketch, "E122.MirrorCS", {"start": v(46.94, -7.5) * mm, "end": v(56.94, -7.5) * mm});
            skLineSegment(sketch, "E123.MirrorCS", {"start": v(46.94, -10) * mm, "end": v(56.94, -10) * mm});
            skLineSegment(sketch, "E124.MirrorCS", {"start": v(46.94, 20.05) * mm, "end": v(56.94, 20.05) * mm});
            skLineSegment(sketch, "E125.MirrorCS", {"start": v(46.94, 37.55) * mm, "end": v(56.94, 37.55) * mm});
            skLineSegment(sketch, "E126.MirrorCS", {"start": v(46.94, 50.05) * mm, "end": v(56.94, 50.05) * mm});
            skLineSegment(sketch, "E127.MirrorCS", {"start": v(46.94, -12.5) * mm, "end": v(56.94, -12.5) * mm});
            skLineSegment(sketch, "E128.MirrorCS", {"start": v(56.94, -25) * mm, "end": v(56.94, -22.5) * mm});
            skLineSegment(sketch, "E129.MirrorCS", {"start": v(46.94, -37.5) * mm, "end": v(56.94, -37.5) * mm});
            skLineSegment(sketch, "E130.MirrorCS", {"start": v(46.94, -15) * mm, "end": v(56.94, -15) * mm});
            skLineSegment(sketch, "E131.MirrorCS", {"start": v(46.94, 0.05) * mm, "end": v(56.94, 0.05) * mm});
            skLineSegment(sketch, "E132.MirrorCS", {"start": v(46.94, 17.55) * mm, "end": v(56.94, 17.55) * mm});
            skLineSegment(sketch, "E133.MirrorCS", {"start": v(46.94, -40) * mm, "end": v(56.94, -40) * mm});
            skLineSegment(sketch, "E134.MirrorCS", {"start": v(46.94, -5) * mm, "end": v(56.94, -5) * mm});
            skLineSegment(sketch, "E135.MirrorCS", {"start": v(46.94, -17.5) * mm, "end": v(56.94, -17.5) * mm});
            skLineSegment(sketch, "E136.MirrorCS", {"start": v(46.94, 45.05) * mm, "end": v(56.94, 45.05) * mm});
            skLineSegment(sketch, "E137.MirrorCS", {"start": v(46.94, 47.55) * mm, "end": v(56.94, 47.55) * mm});
            skLineSegment(sketch, "E138.MirrorCS", {"start": v(46.94, -2.5) * mm, "end": v(56.94, -2.5) * mm});
            skLineSegment(sketch, "E139.MirrorCS", {"start": v(46.94, -20) * mm, "end": v(56.94, -20) * mm});
            skLineSegment(sketch, "E140.MirrorCS", {"start": v(56.94, 40.05) * mm, "end": v(56.94, 42.55) * mm});
            skLineSegment(sketch, "E141.MirrorCS", {"start": v(46.94, 55.05) * mm, "end": v(56.94, 55.05) * mm});
            skLineSegment(sketch, "E142.MirrorCS", {"start": v(46.94, 7.55) * mm, "end": v(56.94, 7.55) * mm});
            skLineSegment(sketch, "E143.MirrorCS", {"start": v(46.94, 5.05) * mm, "end": v(56.94, 5.05) * mm});
            skLineSegment(sketch, "E144.MirrorCS", {"start": v(46.94, -42.5) * mm, "end": v(56.94, -42.5) * mm});
            skLineSegment(sketch, "E145.MirrorCS", {"start": v(46.94, 52.55) * mm, "end": v(56.94, 52.55) * mm});
            skLineSegment(sketch, "E146.MirrorCS", {"start": v(46.94, -45) * mm, "end": v(56.94, -45) * mm});
            skLineSegment(sketch, "E147.MirrorCS", {"start": v(46.94, -27.5) * mm, "end": v(56.94, -27.5) * mm});
            skLineSegment(sketch, "E148.MirrorCS", {"start": v(46.94, 67.55) * mm, "end": v(56.94, 67.55) * mm});
            skLineSegment(sketch, "E149.MirrorCS", {"start": v(46.94, -30) * mm, "end": v(56.94, -30) * mm});
            skLineSegment(sketch, "E150.MirrorCS", {"start": v(46.94, 10.05) * mm, "end": v(56.94, 10.05) * mm});
            skLineSegment(sketch, "E151.MirrorCS", {"start": v(56.94, -40) * mm, "end": v(56.94, -37.5) * mm});
            skLineSegment(sketch, "E152.MirrorCS", {"start": v(46.94, 12.55) * mm, "end": v(56.94, 12.55) * mm});
            skLineSegment(sketch, "E153.MirrorCS", {"start": v(46.94, 15.05) * mm, "end": v(56.94, 15.05) * mm});
            skLineSegment(sketch, "E154.MirrorCS", {"start": v(46.94, -35) * mm, "end": v(56.94, -35) * mm});
            skLineSegment(sketch, "E155.MirrorCS", {"start": v(46.94, 2.55) * mm, "end": v(56.94, 2.55) * mm});
            skLineSegment(sketch, "E156.MirrorCS", {"start": v(46.94, 62.55) * mm, "end": v(56.94, 62.55) * mm});
            skLineSegment(sketch, "E157.MirrorCS", {"start": v(46.94, 57.55) * mm, "end": v(56.94, 57.55) * mm});
            skLineSegment(sketch, "E158.MirrorCS", {"start": v(46.94, 60.05) * mm, "end": v(56.94, 60.05) * mm});
            skLineSegment(sketch, "E159.MirrorCS", {"start": v(46.94, -32.5) * mm, "end": v(56.94, -32.5) * mm});
            skLineSegment(sketch, "E160.MirrorCS", {"start": v(46.94, 65.05) * mm, "end": v(56.94, 65.05) * mm});
            skLineSegment(sketch, "E161.MirrorCS", {"start": v(46.94, 70.05) * mm, "end": v(56.94, 70.05) * mm});
            skLineSegment(sketch, "E162.MirrorCS", {"start": v(46.94, -57.5) * mm, "end": v(56.94, -57.5) * mm});
            skLineSegment(sketch, "E163.MirrorCS", {"start": v(46.94, -52.5) * mm, "end": v(56.94, -52.5) * mm});
            skLineSegment(sketch, "E164.MirrorCS", {"start": v(46.94, -55) * mm, "end": v(56.94, -55) * mm});
            skLineSegment(sketch, "E165.MirrorCS", {"start": v(46.94, -47.5) * mm, "end": v(56.94, -47.5) * mm});
            skLineSegment(sketch, "E166.MirrorCS", {"start": v(46.94, -50) * mm, "end": v(56.94, -50) * mm});
            skLineSegment(sketch, "E167.MirrorCS", {"start": v(46.94, 72.55) * mm, "end": v(56.94, 72.55) * mm});
            skLineSegment(sketch, "E168.MirrorCS", {"start": v(46.94, -60) * mm, "end": v(56.94, -60) * mm});
            skLineSegment(sketch, "E169.MirrorCS", {"start": v(46.94, 80.05) * mm, "end": v(56.94, 80.05) * mm});
            skLineSegment(sketch, "E170.MirrorCS", {"start": v(46.94, -62.5) * mm, "end": v(56.94, -62.5) * mm});
            skLineSegment(sketch, "E171.MirrorCS", {"start": v(46.94, 75.05) * mm, "end": v(56.94, 75.05) * mm});
            skLineSegment(sketch, "E172.MirrorCS", {"start": v(46.94, 77.55) * mm, "end": v(56.94, 77.55) * mm});
            skLineSegment(sketch, "E173.MirrorCS", {"start": v(46.94, -70) * mm, "end": v(56.94, -70) * mm});
            skLineSegment(sketch, "E174.MirrorCS", {"start": v(46.94, -65) * mm, "end": v(56.94, -65) * mm});
            skLineSegment(sketch, "E175.MirrorCS", {"start": v(46.94, -67.5) * mm, "end": v(56.94, -67.5) * mm});
            skLineSegment(sketch, "E176.MirrorCS", {"start": v(56.94, 35.05) * mm, "end": v(56.94, 37.55) * mm});
            skLineSegment(sketch, "E177.MirrorCS", {"start": v(56.94, -45) * mm, "end": v(56.94, -42.5) * mm});
            skLineSegment(sketch, "E178.MirrorCS", {"start": v(46.94, -72.5) * mm, "end": v(56.94, -72.5) * mm});
            skLineSegment(sketch, "E179.MirrorCS", {"start": v(56.94, 50.05) * mm, "end": v(56.94, 52.55) * mm});
            skLineSegment(sketch, "E180.MirrorCS", {"start": v(56.94, -30) * mm, "end": v(56.94, -27.5) * mm});
            skLineSegment(sketch, "E181.MirrorCS", {"start": v(56.94, 0.05) * mm, "end": v(56.94, 2.55) * mm});
            skLineSegment(sketch, "E182.MirrorCS", {"start": v(56.94, -10) * mm, "end": v(56.94, -7.5) * mm});
            skLineSegment(sketch, "E183.MirrorCS", {"start": v(56.94, 45.05) * mm, "end": v(56.94, 47.55) * mm});
            skLineSegment(sketch, "E184.MirrorCS", {"start": v(56.94, 5.05) * mm, "end": v(56.94, 7.55) * mm});
            skLineSegment(sketch, "E185.MirrorCS", {"start": v(56.94, -35) * mm, "end": v(56.94, -32.5) * mm});
            skLineSegment(sketch, "E186.MirrorCS", {"start": v(56.94, 10.05) * mm, "end": v(56.94, 12.55) * mm});
            skLineSegment(sketch, "E187.MirrorCS", {"start": v(56.94, -5) * mm, "end": v(56.94, -2.5) * mm});
            skLineSegment(sketch, "E188.MirrorCS", {"start": v(46.94, 82.55) * mm, "end": v(56.94, 82.55) * mm});
            skLineSegment(sketch, "E189.MirrorCS", {"start": v(56.94, 20.05) * mm, "end": v(56.94, 22.55) * mm});
            skLineSegment(sketch, "E190.MirrorCS", {"start": v(46.94, 87.55) * mm, "end": v(56.94, 87.55) * mm});
            skLineSegment(sketch, "E191.MirrorCS", {"start": v(46.94, 85.05) * mm, "end": v(56.94, 85.05) * mm});
            skLineSegment(sketch, "E192.MirrorCS", {"start": v(46.94, -75) * mm, "end": v(56.94, -75) * mm});
            skLineSegment(sketch, "E193.MirrorCS", {"start": v(56.94, -15) * mm, "end": v(56.94, -12.5) * mm});
            skLineSegment(sketch, "E194.MirrorCS", {"start": v(56.94, 15.05) * mm, "end": v(56.94, 17.55) * mm});
            skLineSegment(sketch, "E195.MirrorCS", {"start": v(46.94, -77.5) * mm, "end": v(56.94, -77.5) * mm});
            skLineSegment(sketch, "E196.MirrorCS", {"start": v(56.94, -20) * mm, "end": v(56.94, -17.5) * mm});
            skLineSegment(sketch, "E197.MirrorCS", {"start": v(56.94, 30.05) * mm, "end": v(56.94, 32.55) * mm});
            skLineSegment(sketch, "E198.MirrorCS", {"start": v(56.94, 65.05) * mm, "end": v(56.94, 67.55) * mm});
            skLineSegment(sketch, "E199.MirrorCS", {"start": v(56.94, 55.05) * mm, "end": v(56.94, 57.55) * mm});
            skLineSegment(sketch, "E200.MirrorCS", {"start": v(56.94, 60.05) * mm, "end": v(56.94, 62.55) * mm});
            skLineSegment(sketch, "E201.MirrorCS", {"start": v(56.94, -60) * mm, "end": v(56.94, -57.5) * mm});
            skLineSegment(sketch, "E202.MirrorCS", {"start": v(56.94, 70.05) * mm, "end": v(56.94, 72.55) * mm});
            skLineSegment(sketch, "E203.MirrorCS", {"start": v(56.94, -50) * mm, "end": v(56.94, -47.5) * mm});
            skLineSegment(sketch, "E204.MirrorCS", {"start": v(56.94, -55) * mm, "end": v(56.94, -52.5) * mm});
            skLineSegment(sketch, "E205.MirrorCS", {"start": v(56.94, 75.05) * mm, "end": v(56.94, 77.55) * mm});
            skLineSegment(sketch, "E206.MirrorCS", {"start": v(56.94, 80.05) * mm, "end": v(56.94, 82.55) * mm});
            skLineSegment(sketch, "E207.MirrorCS", {"start": v(56.94, -65) * mm, "end": v(56.94, -62.5) * mm});
            skLineSegment(sketch, "E208.MirrorCS", {"start": v(56.94, 85.05) * mm, "end": v(56.94, 87.55) * mm});
            skLineSegment(sketch, "E209.MirrorCS", {"start": v(56.94, -70) * mm, "end": v(56.94, -67.5) * mm});
            skLineSegment(sketch, "E210.MirrorCS", {"start": v(56.94, -80) * mm, "end": v(56.94, -77.5) * mm});
            skLineSegment(sketch, "E211.MirrorCS", {"start": v(46.94, -80) * mm, "end": v(56.94, -80) * mm});
            skLineSegment(sketch, "E212.MirrorCS", {"start": v(56.94, -75) * mm, "end": v(56.94, -72.5) * mm});
            skLineSegment(sketch, "E213", {"start": v(46.94, -80) * mm, "end": v(46.94, 87.55) * mm});
            skSolve(sketch);
        }
        {
            var Q0;
            Q0 = qSketchRegion(id + "F6", true);
            var Q1;
            {var subQ0=sQuery(id+"F0.wireOp",EDGE,"E3.left");var subQ1=sQuery(id+"F0.wireOp",EDGE,"E3.bottom");Q1=makeQuery(id+"F4.boolean.opBoolean","MERGE",FACE,{"derivedFrom":[makeQuery(id+"F2.boolean.opBoolean","MERGE",FACE,{"derivedFrom":[makeQuery(id+"F1.opExtrude","CAP_FACE",FACE,{"disambiguationData":[OSD([sQuery(id+"F0.wireOp",EDGE,"E0.top"),sQuery(id+"F0.wireOp",EDGE,"E0.left"),sQuery(id+"F0.wireOp",EDGE,"E0.right"),subQ1,subQ0,sQuery(id+"F0.wireOp",EDGE,"E3.right"),sQuery(id+"F0.wireOp",EDGE,"E4")])],"isStart":true}),makeQuery(id+"F2.opExtrude","SWEPT_FACE",FACE,{"disambiguationData":[OSD([subQ1]),TDD([makeQuery(id+"F1.opExtrude","CAP_EDGE",EDGE,{"disambiguationData":[OSD([subQ1])],"isStart":true})])]})]}),makeQuery(id+"F4.opExtrude","SWEPT_FACE",FACE,{"disambiguationData":[OSD([subQ1,subQ0]),TDD([makeQuery(id+"F2.boolean.opBoolean","MERGE",EDGE,{"derivedFrom":[makeQuery(id+"F1.opExtrude","CAP_EDGE",EDGE,{"disambiguationData":[OSD([subQ0])],"isStart":true}),makeQuery(id+"F2.opExtrude","SWEPT_EDGE",EDGE,{"disambiguationData":[OSD([subQ1,subQ0]),TDD([makeQuery(id+"F1.opExtrude","CAP_VERTEX",VERTEX,{"disambiguationData":[OSD([subQ1,subQ0])],"isStart":true})])]})]})])]})]});}
            extrude(context, id + "F7", {"entities" : qUnion([Q0]), "operationType" : NewBodyOperationType.ADD, "endBound" : BoundingType.UP_TO_SURFACE, "oppositeDirection" : true, "depth" : 25 * mm, "endBoundEntityFace" : qUnion([Q1]), "offsetDistance" : 25 * mm});
        }
        {
            var Q0;
            {var subQ0=sQuery(id+"F0.wireOp",EDGE,"E4");Q0=makeQuery(id+"F7.boolean.opBoolean","MERGE",FACE,{"derivedFrom":[makeQuery(id+"F1.opExtrude","SWEPT_FACE",FACE,{"disambiguationData":[OSD([subQ0]),TDD([makeQuery(id+"F0.imprint","IMPRINT",EDGE,{"disambiguationData":[TD([[makeQuery(id+"F0.imprint","INTERSECT",VERTEX,{"derivedFrom":[sQuery(id+"F0.wireOp",EDGE,"E0.right"),subQ0]}),1.0]])],"derivedFrom":subQ0})])]}),makeQuery(id+"F7.opExtrude","SWEPT_FACE",FACE,{"disambiguationData":[OSD([sQuery(id+"F6.wireOp",EDGE,"E5.bottom")])]})]});}
            extrude(context, id + "F8", {"entities" : qUnion([Q0]), "operationType" : NewBodyOperationType.REMOVE, "oppositeDirection" : true, "depth" : 1.25 * mm, "offsetDistance" : 25 * mm});
        }
        {
            var Q0;
            Q0=makeQuery(id+"F1.opExtrude","SWEPT_BODY",BODY,{"disambiguationData":[OSD([sQuery(id+"F0.wireOp",EDGE,"E0.top"),sQuery(id+"F0.wireOp",EDGE,"E0.left"),sQuery(id+"F0.wireOp",EDGE,"E0.right"),sQuery(id+"F0.wireOp",EDGE,"E3.bottom"),sQuery(id+"F0.wireOp",EDGE,"E3.left"),sQuery(id+"F0.wireOp",EDGE,"E3.right"),sQuery(id+"F0.wireOp",EDGE,"E4")])]});
            var Q1;
            Q1=makeQuery(id+"F8.boolean.opBoolean","COPY",FACE,{"derivedFrom":makeQuery(id+"F8.opExtrude","CAP_FACE",FACE,{"disambiguationData":[OSD([sQuery(id+"F0.wireOp",EDGE,"E4"),sQuery(id+"F6.wireOp",EDGE,"E5.bottom")])],"isStart":false})});
            mirror(context, id + "F9", {"operationType" : NewBodyOperationType.ADD, "entities" : qUnion([Q0]), "mirrorPlane" : qUnion([Q1])});
        }
        {
            var Q0;
            {var subQ0=sQuery(id+"F6.wireOp",EDGE,"E213");var subQ1=sQuery(id+"F0.wireOp",EDGE,"E3.left");var subQ2=sQuery(id+"F0.wireOp",EDGE,"E3.bottom");var subQ3=makeQuery(id+"F7.boolean.opBoolean","MERGE",FACE,{"derivedFrom":[makeQuery(id+"F4.boolean.opBoolean","MERGE",FACE,{"derivedFrom":[makeQuery(id+"F2.boolean.opBoolean","MERGE",FACE,{"derivedFrom":[makeQuery(id+"F1.opExtrude","CAP_FACE",FACE,{"disambiguationData":[OSD([sQuery(id+"F0.wireOp",EDGE,"E0.top"),sQuery(id+"F0.wireOp",EDGE,"E0.left"),sQuery(id+"F0.wireOp",EDGE,"E0.right"),subQ2,subQ1,sQuery(id+"F0.wireOp",EDGE,"E3.right"),sQuery(id+"F0.wireOp",EDGE,"E4")])],"isStart":true}),makeQuery(id+"F2.opExtrude","SWEPT_FACE",FACE,{"disambiguationData":[OSD([subQ2]),TDD([makeQuery(id+"F1.opExtrude","CAP_EDGE",EDGE,{"disambiguationData":[OSD([subQ2])],"isStart":true})])]})]}),makeQuery(id+"F4.opExtrude","SWEPT_FACE",FACE,{"disambiguationData":[OSD([subQ2,subQ1]),TDD([makeQuery(id+"F2.boolean.opBoolean","MERGE",EDGE,{"derivedFrom":[makeQuery(id+"F1.opExtrude","CAP_EDGE",EDGE,{"disambiguationData":[OSD([subQ1])],"isStart":true}),makeQuery(id+"F2.opExtrude","SWEPT_EDGE",EDGE,{"disambiguationData":[OSD([subQ2,subQ1]),TDD([makeQuery(id+"F1.opExtrude","CAP_VERTEX",VERTEX,{"disambiguationData":[OSD([subQ2,subQ1])],"isStart":true})])]})]})])]})]}),makeQuery(id+"F7.opExtrude","CAP_FACE",FACE,{"disambiguationData":[OSD([sQuery(id+"F6.wireOp",EDGE,"E5.bottom"),sQuery(id+"F6.wireOp",EDGE,"E5.top"),sQuery(id+"F6.wireOp",EDGE,"E5.left"),sQuery(id+"F6.wireOp",EDGE,"E5.right")])],"isStart":false}),makeQuery(id+"F7.opExtrude","CAP_FACE",FACE,{"disambiguationData":[OSD([sQuery(id+"F6.wireOp",EDGE,"E7.bottom"),sQuery(id+"F6.wireOp",EDGE,"E7.top"),sQuery(id+"F6.wireOp",EDGE,"E7.left"),sQuery(id+"F6.wireOp",EDGE,"E7.right")])],"isStart":false}),makeQuery(id+"F7.opExtrude","CAP_FACE",FACE,{"disambiguationData":[OSD([sQuery(id+"F6.wireOp",EDGE,"E9.bottom"),sQuery(id+"F6.wireOp",EDGE,"E9.top"),sQuery(id+"F6.wireOp",EDGE,"E9.left"),sQuery(id+"F6.wireOp",EDGE,"E9.right")])],"isStart":false}),makeQuery(id+"F7.opExtrude","CAP_FACE",FACE,{"disambiguationData":[OSD([sQuery(id+"F6.wireOp",EDGE,"E11.bottom"),sQuery(id+"F6.wireOp",EDGE,"E11.top"),sQuery(id+"F6.wireOp",EDGE,"E11.left"),sQuery(id+"F6.wireOp",EDGE,"E11.right")])],"isStart":false}),makeQuery(id+"F7.opExtrude","CAP_FACE",FACE,{"disambiguationData":[OSD([sQuery(id+"F6.wireOp",EDGE,"E13.bottom"),sQuery(id+"F6.wireOp",EDGE,"E13.top"),sQuery(id+"F6.wireOp",EDGE,"E13.left"),sQuery(id+"F6.wireOp",EDGE,"E13.right")])],"isStart":false}),makeQuery(id+"F7.opExtrude","CAP_FACE",FACE,{"disambiguationData":[OSD([sQuery(id+"F6.wireOp",EDGE,"E15.bottom"),sQuery(id+"F6.wireOp",EDGE,"E15.top"),sQuery(id+"F6.wireOp",EDGE,"E15.left"),sQuery(id+"F6.wireOp",EDGE,"E15.right")])],"isStart":false}),makeQuery(id+"F7.opExtrude","CAP_FACE",FACE,{"disambiguationData":[OSD([sQuery(id+"F6.wireOp",EDGE,"E17.bottom"),sQuery(id+"F6.wireOp",EDGE,"E17.top"),sQuery(id+"F6.wireOp",EDGE,"E17.left"),sQuery(id+"F6.wireOp",EDGE,"E17.right")])],"isStart":false}),makeQuery(id+"F7.opExtrude","CAP_FACE",FACE,{"disambiguationData":[OSD([sQuery(id+"F6.wireOp",EDGE,"E19.bottom"),sQuery(id+"F6.wireOp",EDGE,"E19.top"),sQuery(id+"F6.wireOp",EDGE,"E19.left"),sQuery(id+"F6.wireOp",EDGE,"E19.right")])],"isStart":false}),makeQuery(id+"F7.opExtrude","CAP_FACE",FACE,{"disambiguationData":[OSD([sQuery(id+"F6.wireOp",EDGE,"E21.bottom"),sQuery(id+"F6.wireOp",EDGE,"E21.top"),sQuery(id+"F6.wireOp",EDGE,"E21.left"),sQuery(id+"F6.wireOp",EDGE,"E21.right")])],"isStart":false}),makeQuery(id+"F7.opExtrude","CAP_FACE",FACE,{"disambiguationData":[OSD([sQuery(id+"F6.wireOp",EDGE,"E23.bottom"),sQuery(id+"F6.wireOp",EDGE,"E23.top"),sQuery(id+"F6.wireOp",EDGE,"E23.left"),sQuery(id+"F6.wireOp",EDGE,"E23.right")])],"isStart":false}),makeQuery(id+"F7.opExtrude","CAP_FACE",FACE,{"disambiguationData":[OSD([sQuery(id+"F6.wireOp",EDGE,"E25.bottom"),sQuery(id+"F6.wireOp",EDGE,"E25.top"),sQuery(id+"F6.wireOp",EDGE,"E25.left"),sQuery(id+"F6.wireOp",EDGE,"E25.right")])],"isStart":false}),makeQuery(id+"F7.opExtrude","CAP_FACE",FACE,{"disambiguationData":[OSD([sQuery(id+"F6.wireOp",EDGE,"E27.bottom"),sQuery(id+"F6.wireOp",EDGE,"E27.top"),sQuery(id+"F6.wireOp",EDGE,"E27.left"),sQuery(id+"F6.wireOp",EDGE,"E27.right")])],"isStart":false}),makeQuery(id+"F7.opExtrude","CAP_FACE",FACE,{"disambiguationData":[OSD([sQuery(id+"F6.wireOp",EDGE,"E29.bottom"),sQuery(id+"F6.wireOp",EDGE,"E29.top"),sQuery(id+"F6.wireOp",EDGE,"E29.left"),sQuery(id+"F6.wireOp",EDGE,"E29.right")])],"isStart":false}),makeQuery(id+"F7.opExtrude","CAP_FACE",FACE,{"disambiguationData":[OSD([sQuery(id+"F6.wireOp",EDGE,"E31.bottom"),sQuery(id+"F6.wireOp",EDGE,"E31.top"),sQuery(id+"F6.wireOp",EDGE,"E31.left"),sQuery(id+"F6.wireOp",EDGE,"E31.right")])],"isStart":false}),makeQuery(id+"F7.opExtrude","CAP_FACE",FACE,{"disambiguationData":[OSD([sQuery(id+"F6.wireOp",EDGE,"E33.bottom"),sQuery(id+"F6.wireOp",EDGE,"E33.top"),sQuery(id+"F6.wireOp",EDGE,"E33.left"),sQuery(id+"F6.wireOp",EDGE,"E33.right")])],"isStart":false}),makeQuery(id+"F7.opExtrude","CAP_FACE",FACE,{"disambiguationData":[OSD([sQuery(id+"F6.wireOp",EDGE,"E35.bottom"),sQuery(id+"F6.wireOp",EDGE,"E35.top"),sQuery(id+"F6.wireOp",EDGE,"E35.left"),sQuery(id+"F6.wireOp",EDGE,"E35.right")])],"isStart":false}),makeQuery(id+"F7.opExtrude","CAP_FACE",FACE,{"disambiguationData":[OSD([sQuery(id+"F6.wireOp",EDGE,"E37.bottom"),sQuery(id+"F6.wireOp",EDGE,"E37.top"),sQuery(id+"F6.wireOp",EDGE,"E37.left"),sQuery(id+"F6.wireOp",EDGE,"E37.right")])],"isStart":false}),makeQuery(id+"F7.opExtrude","CAP_FACE",FACE,{"disambiguationData":[OSD([sQuery(id+"F6.wireOp",EDGE,"E39.bottom"),sQuery(id+"F6.wireOp",EDGE,"E39.top"),sQuery(id+"F6.wireOp",EDGE,"E39.left"),sQuery(id+"F6.wireOp",EDGE,"E39.right")])],"isStart":false}),makeQuery(id+"F7.opExtrude","CAP_FACE",FACE,{"disambiguationData":[OSD([sQuery(id+"F6.wireOp",EDGE,"E41.bottom"),sQuery(id+"F6.wireOp",EDGE,"E41.top"),sQuery(id+"F6.wireOp",EDGE,"E41.left"),sQuery(id+"F6.wireOp",EDGE,"E41.right")])],"isStart":false}),makeQuery(id+"F7.opExtrude","CAP_FACE",FACE,{"disambiguationData":[OSD([sQuery(id+"F6.wireOp",EDGE,"E43.bottom"),sQuery(id+"F6.wireOp",EDGE,"E43.top"),sQuery(id+"F6.wireOp",EDGE,"E43.left"),sQuery(id+"F6.wireOp",EDGE,"E43.right")])],"isStart":false}),makeQuery(id+"F7.opExtrude","CAP_FACE",FACE,{"disambiguationData":[OSD([sQuery(id+"F6.wireOp",EDGE,"E45.bottom"),sQuery(id+"F6.wireOp",EDGE,"E45.top"),sQuery(id+"F6.wireOp",EDGE,"E45.left"),sQuery(id+"F6.wireOp",EDGE,"E45.right")])],"isStart":false}),makeQuery(id+"F7.opExtrude","CAP_FACE",FACE,{"disambiguationData":[OSD([sQuery(id+"F6.wireOp",EDGE,"E47.bottom"),sQuery(id+"F6.wireOp",EDGE,"E47.top"),sQuery(id+"F6.wireOp",EDGE,"E47.left"),sQuery(id+"F6.wireOp",EDGE,"E47.right")])],"isStart":false}),makeQuery(id+"F7.opExtrude","CAP_FACE",FACE,{"disambiguationData":[OSD([sQuery(id+"F6.wireOp",EDGE,"E49.bottom"),sQuery(id+"F6.wireOp",EDGE,"E49.top"),sQuery(id+"F6.wireOp",EDGE,"E49.left"),sQuery(id+"F6.wireOp",EDGE,"E49.right")])],"isStart":false}),makeQuery(id+"F7.opExtrude","CAP_FACE",FACE,{"disambiguationData":[OSD([sQuery(id+"F6.wireOp",EDGE,"E51.bottom"),sQuery(id+"F6.wireOp",EDGE,"E51.top"),sQuery(id+"F6.wireOp",EDGE,"E51.left"),sQuery(id+"F6.wireOp",EDGE,"E51.right")])],"isStart":false}),makeQuery(id+"F7.opExtrude","CAP_FACE",FACE,{"disambiguationData":[OSD([sQuery(id+"F6.wireOp",EDGE,"E53.bottom"),sQuery(id+"F6.wireOp",EDGE,"E53.top"),sQuery(id+"F6.wireOp",EDGE,"E53.left"),sQuery(id+"F6.wireOp",EDGE,"E53.right")])],"isStart":false}),makeQuery(id+"F7.opExtrude","CAP_FACE",FACE,{"disambiguationData":[OSD([sQuery(id+"F6.wireOp",EDGE,"E55.bottom"),sQuery(id+"F6.wireOp",EDGE,"E55.top"),sQuery(id+"F6.wireOp",EDGE,"E55.left"),sQuery(id+"F6.wireOp",EDGE,"E55.right")])],"isStart":false}),makeQuery(id+"F7.opExtrude","CAP_FACE",FACE,{"disambiguationData":[OSD([sQuery(id+"F6.wireOp",EDGE,"E57.bottom"),sQuery(id+"F6.wireOp",EDGE,"E57.top"),sQuery(id+"F6.wireOp",EDGE,"E57.left"),sQuery(id+"F6.wireOp",EDGE,"E57.right")])],"isStart":false}),makeQuery(id+"F7.opExtrude","CAP_FACE",FACE,{"disambiguationData":[OSD([sQuery(id+"F6.wireOp",EDGE,"E59.bottom"),sQuery(id+"F6.wireOp",EDGE,"E59.top"),sQuery(id+"F6.wireOp",EDGE,"E59.left"),sQuery(id+"F6.wireOp",EDGE,"E59.right")])],"isStart":false}),makeQuery(id+"F7.opExtrude","CAP_FACE",FACE,{"disambiguationData":[OSD([sQuery(id+"F6.wireOp",EDGE,"E61.bottom"),sQuery(id+"F6.wireOp",EDGE,"E61.top"),sQuery(id+"F6.wireOp",EDGE,"E61.left"),sQuery(id+"F6.wireOp",EDGE,"E61.right")])],"isStart":false}),makeQuery(id+"F7.opExtrude","CAP_FACE",FACE,{"disambiguationData":[OSD([sQuery(id+"F6.wireOp",EDGE,"E63.bottom"),sQuery(id+"F6.wireOp",EDGE,"E63.top"),sQuery(id+"F6.wireOp",EDGE,"E63.left"),sQuery(id+"F6.wireOp",EDGE,"E63.right")])],"isStart":false}),makeQuery(id+"F7.opExtrude","CAP_FACE",FACE,{"disambiguationData":[OSD([sQuery(id+"F6.wireOp",EDGE,"E65.bottom"),sQuery(id+"F6.wireOp",EDGE,"E65.top"),sQuery(id+"F6.wireOp",EDGE,"E65.left"),sQuery(id+"F6.wireOp",EDGE,"E65.right")])],"isStart":false}),makeQuery(id+"F7.opExtrude","CAP_FACE",FACE,{"disambiguationData":[OSD([sQuery(id+"F6.wireOp",EDGE,"E67.bottom"),sQuery(id+"F6.wireOp",EDGE,"E67.top"),sQuery(id+"F6.wireOp",EDGE,"E67.left"),sQuery(id+"F6.wireOp",EDGE,"E67.right")])],"isStart":false}),makeQuery(id+"F7.opExtrude","CAP_FACE",FACE,{"disambiguationData":[OSD([sQuery(id+"F6.wireOp",EDGE,"E69.bottom"),sQuery(id+"F6.wireOp",EDGE,"E69.top"),sQuery(id+"F6.wireOp",EDGE,"E69.left"),sQuery(id+"F6.wireOp",EDGE,"E69.right")])],"isStart":false}),makeQuery(id+"F7.opExtrude","CAP_FACE",FACE,{"disambiguationData":[OSD([sQuery(id+"F6.wireOp",EDGE,"E71.bottom"),sQuery(id+"F6.wireOp",EDGE,"E71.top"),sQuery(id+"F6.wireOp",EDGE,"E71.right"),sQuery(id+"F6.wireOp",EDGE,"E72.bottom"),sQuery(id+"F6.wireOp",EDGE,"E72.top"),sQuery(id+"F6.wireOp",EDGE,"E72.left"),sQuery(id+"F6.wireOp",EDGE,"E72.right")])],"isStart":false}),makeQuery(id+"F7.opExtrude","CAP_FACE",FACE,{"disambiguationData":[OSD([sQuery(id+"F6.wireOp",EDGE,"E74.bottom"),sQuery(id+"F6.wireOp",EDGE,"E74.top"),sQuery(id+"F6.wireOp",EDGE,"E74.left"),sQuery(id+"F6.wireOp",EDGE,"E74.right")])],"isStart":false}),makeQuery(id+"F7.opExtrude","CAP_FACE",FACE,{"disambiguationData":[OSD([sQuery(id+"F6.wireOp",EDGE,"E76.bottom"),sQuery(id+"F6.wireOp",EDGE,"E76.top"),sQuery(id+"F6.wireOp",EDGE,"E76.left"),sQuery(id+"F6.wireOp",EDGE,"E76.right")])],"isStart":false}),makeQuery(id+"F7.opExtrude","CAP_FACE",FACE,{"disambiguationData":[OSD([sQuery(id+"F6.wireOp",EDGE,"E78.bottom"),sQuery(id+"F6.wireOp",EDGE,"E78.top"),sQuery(id+"F6.wireOp",EDGE,"E78.left"),sQuery(id+"F6.wireOp",EDGE,"E78.right")])],"isStart":false}),makeQuery(id+"F7.opExtrude","CAP_FACE",FACE,{"disambiguationData":[OSD([sQuery(id+"F6.wireOp",EDGE,"E80.bottom"),sQuery(id+"F6.wireOp",EDGE,"E80.top"),sQuery(id+"F6.wireOp",EDGE,"E80.left"),sQuery(id+"F6.wireOp",EDGE,"E80.right")])],"isStart":false}),makeQuery(id+"F7.opExtrude","CAP_FACE",FACE,{"disambiguationData":[OSD([sQuery(id+"F6.wireOp",EDGE,"E82.bottom"),sQuery(id+"F6.wireOp",EDGE,"E82.top"),sQuery(id+"F6.wireOp",EDGE,"E82.left"),sQuery(id+"F6.wireOp",EDGE,"E82.right")])],"isStart":false}),makeQuery(id+"F7.opExtrude","CAP_FACE",FACE,{"disambiguationData":[OSD([sQuery(id+"F6.wireOp",EDGE,"E84.bottom"),sQuery(id+"F6.wireOp",EDGE,"E84.top"),sQuery(id+"F6.wireOp",EDGE,"E84.left"),sQuery(id+"F6.wireOp",EDGE,"E84.right")])],"isStart":false}),makeQuery(id+"F7.opExtrude","CAP_FACE",FACE,{"disambiguationData":[OSD([sQuery(id+"F6.wireOp",EDGE,"E86.bottom"),sQuery(id+"F6.wireOp",EDGE,"E86.top"),sQuery(id+"F6.wireOp",EDGE,"E86.left"),sQuery(id+"F6.wireOp",EDGE,"E86.right")])],"isStart":false}),makeQuery(id+"F7.opExtrude","CAP_FACE",FACE,{"disambiguationData":[OSD([sQuery(id+"F6.wireOp",EDGE,"E88.bottom"),sQuery(id+"F6.wireOp",EDGE,"E88.top"),sQuery(id+"F6.wireOp",EDGE,"E88.left"),sQuery(id+"F6.wireOp",EDGE,"E88.right")])],"isStart":false}),makeQuery(id+"F7.opExtrude","CAP_FACE",FACE,{"disambiguationData":[OSD([sQuery(id+"F6.wireOp",EDGE,"E90.bottom"),sQuery(id+"F6.wireOp",EDGE,"E90.top"),sQuery(id+"F6.wireOp",EDGE,"E90.left"),sQuery(id+"F6.wireOp",EDGE,"E90.right")])],"isStart":false}),makeQuery(id+"F7.opExtrude","CAP_FACE",FACE,{"disambiguationData":[OSD([sQuery(id+"F6.wireOp",EDGE,"E92.bottom"),sQuery(id+"F6.wireOp",EDGE,"E92.top"),sQuery(id+"F6.wireOp",EDGE,"E92.left"),sQuery(id+"F6.wireOp",EDGE,"E92.right")])],"isStart":false}),makeQuery(id+"F7.opExtrude","CAP_FACE",FACE,{"disambiguationData":[OSD([sQuery(id+"F6.wireOp",EDGE,"E94.bottom"),sQuery(id+"F6.wireOp",EDGE,"E94.top"),sQuery(id+"F6.wireOp",EDGE,"E94.left"),sQuery(id+"F6.wireOp",EDGE,"E94.right")])],"isStart":false}),makeQuery(id+"F7.opExtrude","CAP_FACE",FACE,{"disambiguationData":[OSD([sQuery(id+"F6.wireOp",EDGE,"E96.bottom"),sQuery(id+"F6.wireOp",EDGE,"E96.top"),sQuery(id+"F6.wireOp",EDGE,"E96.left"),sQuery(id+"F6.wireOp",EDGE,"E96.right")])],"isStart":false}),makeQuery(id+"F7.opExtrude","CAP_FACE",FACE,{"disambiguationData":[OSD([sQuery(id+"F6.wireOp",EDGE,"E98.bottom"),sQuery(id+"F6.wireOp",EDGE,"E98.top"),sQuery(id+"F6.wireOp",EDGE,"E98.left"),sQuery(id+"F6.wireOp",EDGE,"E98.right")])],"isStart":false}),makeQuery(id+"F7.opExtrude","CAP_FACE",FACE,{"disambiguationData":[OSD([sQuery(id+"F6.wireOp",EDGE,"E100.bottom"),sQuery(id+"F6.wireOp",EDGE,"E100.top"),sQuery(id+"F6.wireOp",EDGE,"E100.left"),sQuery(id+"F6.wireOp",EDGE,"E100.right")])],"isStart":false}),makeQuery(id+"F7.opExtrude","CAP_FACE",FACE,{"disambiguationData":[OSD([sQuery(id+"F6.wireOp",EDGE,"E102.bottom"),sQuery(id+"F6.wireOp",EDGE,"E102.top"),sQuery(id+"F6.wireOp",EDGE,"E102.left"),sQuery(id+"F6.wireOp",EDGE,"E102.right")])],"isStart":false}),makeQuery(id+"F7.opExtrude","CAP_FACE",FACE,{"disambiguationData":[OSD([sQuery(id+"F6.wireOp",EDGE,"E104.bottom"),sQuery(id+"F6.wireOp",EDGE,"E104.top"),sQuery(id+"F6.wireOp",EDGE,"E104.left"),sQuery(id+"F6.wireOp",EDGE,"E104.right")])],"isStart":false}),makeQuery(id+"F7.opExtrude","CAP_FACE",FACE,{"disambiguationData":[OSD([sQuery(id+"F6.wireOp",EDGE,"E106.bottom"),sQuery(id+"F6.wireOp",EDGE,"E106.top"),sQuery(id+"F6.wireOp",EDGE,"E106.left"),sQuery(id+"F6.wireOp",EDGE,"E106.right")])],"isStart":false}),makeQuery(id+"F7.opExtrude","CAP_FACE",FACE,{"disambiguationData":[OSD([sQuery(id+"F6.wireOp",EDGE,"E108.top"),sQuery(id+"F6.wireOp",EDGE,"E108.left"),sQuery(id+"F6.wireOp",EDGE,"E109"),sQuery(id+"F6.wireOp",EDGE,"E110"),sQuery(id+"F6.wireOp",EDGE,"E191.MirrorCS"),sQuery(id+"F6.wireOp",EDGE,"E190.MirrorCS"),sQuery(id+"F6.wireOp",EDGE,"E208.MirrorCS")])],"isStart":false}),makeQuery(id+"F7.opExtrude","CAP_FACE",FACE,{"disambiguationData":[OSD([sQuery(id+"F6.wireOp",EDGE,"E180.MirrorCS"),sQuery(id+"F6.wireOp",EDGE,"E147.MirrorCS"),sQuery(id+"F6.wireOp",EDGE,"E149.MirrorCS"),subQ0])],"isStart":false}),makeQuery(id+"F7.opExtrude","CAP_FACE",FACE,{"disambiguationData":[OSD([sQuery(id+"F6.wireOp",EDGE,"E179.MirrorCS"),sQuery(id+"F6.wireOp",EDGE,"E145.MirrorCS"),sQuery(id+"F6.wireOp",EDGE,"E126.MirrorCS"),subQ0])],"isStart":false}),makeQuery(id+"F7.opExtrude","CAP_FACE",FACE,{"disambiguationData":[OSD([sQuery(id+"F6.wireOp",EDGE,"E113.MirrorCS"),sQuery(id+"F6.wireOp",EDGE,"E124.MirrorCS"),sQuery(id+"F6.wireOp",EDGE,"E189.MirrorCS"),subQ0])],"isStart":false}),makeQuery(id+"F7.opExtrude","CAP_FACE",FACE,{"disambiguationData":[OSD([sQuery(id+"F6.wireOp",EDGE,"E177.MirrorCS"),sQuery(id+"F6.wireOp",EDGE,"E144.MirrorCS"),sQuery(id+"F6.wireOp",EDGE,"E146.MirrorCS"),subQ0])],"isStart":false}),makeQuery(id+"F7.opExtrude","CAP_FACE",FACE,{"disambiguationData":[OSD([sQuery(id+"F6.wireOp",EDGE,"E176.MirrorCS"),sQuery(id+"F6.wireOp",EDGE,"E125.MirrorCS"),sQuery(id+"F6.wireOp",EDGE,"E114.MirrorCS"),subQ0])],"isStart":false}),makeQuery(id+"F7.opExtrude","CAP_FACE",FACE,{"disambiguationData":[OSD([sQuery(id+"F6.wireOp",EDGE,"E121.MirrorCS"),sQuery(id+"F6.wireOp",EDGE,"E116.MirrorCS"),sQuery(id+"F6.wireOp",EDGE,"E128.MirrorCS"),subQ0])],"isStart":false}),makeQuery(id+"F7.opExtrude","CAP_FACE",FACE,{"disambiguationData":[OSD([sQuery(id+"F6.wireOp",EDGE,"E133.MirrorCS"),sQuery(id+"F6.wireOp",EDGE,"E151.MirrorCS"),sQuery(id+"F6.wireOp",EDGE,"E129.MirrorCS"),subQ0])],"isStart":false}),makeQuery(id+"F7.opExtrude","CAP_FACE",FACE,{"disambiguationData":[OSD([sQuery(id+"F6.wireOp",EDGE,"E193.MirrorCS"),sQuery(id+"F6.wireOp",EDGE,"E127.MirrorCS"),sQuery(id+"F6.wireOp",EDGE,"E130.MirrorCS"),subQ0])],"isStart":false}),makeQuery(id+"F7.opExtrude","CAP_FACE",FACE,{"disambiguationData":[OSD([sQuery(id+"F6.wireOp",EDGE,"E181.MirrorCS"),sQuery(id+"F6.wireOp",EDGE,"E155.MirrorCS"),sQuery(id+"F6.wireOp",EDGE,"E131.MirrorCS"),subQ0])],"isStart":false}),makeQuery(id+"F7.opExtrude","CAP_FACE",FACE,{"disambiguationData":[OSD([sQuery(id+"F6.wireOp",EDGE,"E194.MirrorCS"),sQuery(id+"F6.wireOp",EDGE,"E132.MirrorCS"),sQuery(id+"F6.wireOp",EDGE,"E153.MirrorCS"),subQ0])],"isStart":false}),makeQuery(id+"F7.opExtrude","CAP_FACE",FACE,{"disambiguationData":[OSD([sQuery(id+"F6.wireOp",EDGE,"E197.MirrorCS"),sQuery(id+"F6.wireOp",EDGE,"E117.MirrorCS"),sQuery(id+"F6.wireOp",EDGE,"E120.MirrorCS"),subQ0])],"isStart":false}),makeQuery(id+"F7.opExtrude","CAP_FACE",FACE,{"disambiguationData":[OSD([sQuery(id+"F6.wireOp",EDGE,"E183.MirrorCS"),sQuery(id+"F6.wireOp",EDGE,"E136.MirrorCS"),sQuery(id+"F6.wireOp",EDGE,"E137.MirrorCS"),subQ0])],"isStart":false}),makeQuery(id+"F7.opExtrude","CAP_FACE",FACE,{"disambiguationData":[OSD([sQuery(id+"F6.wireOp",EDGE,"E196.MirrorCS"),sQuery(id+"F6.wireOp",EDGE,"E135.MirrorCS"),sQuery(id+"F6.wireOp",EDGE,"E139.MirrorCS"),subQ0])],"isStart":false}),makeQuery(id+"F7.opExtrude","CAP_FACE",FACE,{"disambiguationData":[OSD([sQuery(id+"F6.wireOp",EDGE,"E143.MirrorCS"),sQuery(id+"F6.wireOp",EDGE,"E142.MirrorCS"),sQuery(id+"F6.wireOp",EDGE,"E184.MirrorCS"),subQ0])],"isStart":false}),makeQuery(id+"F7.opExtrude","CAP_FACE",FACE,{"disambiguationData":[OSD([sQuery(id+"F6.wireOp",EDGE,"E123.MirrorCS"),sQuery(id+"F6.wireOp",EDGE,"E122.MirrorCS"),sQuery(id+"F6.wireOp",EDGE,"E182.MirrorCS"),subQ0])],"isStart":false}),makeQuery(id+"F7.opExtrude","CAP_FACE",FACE,{"disambiguationData":[OSD([sQuery(id+"F6.wireOp",EDGE,"E186.MirrorCS"),sQuery(id+"F6.wireOp",EDGE,"E150.MirrorCS"),sQuery(id+"F6.wireOp",EDGE,"E152.MirrorCS"),subQ0])],"isStart":false}),makeQuery(id+"F7.opExtrude","CAP_FACE",FACE,{"disambiguationData":[OSD([sQuery(id+"F6.wireOp",EDGE,"E154.MirrorCS"),sQuery(id+"F6.wireOp",EDGE,"E159.MirrorCS"),sQuery(id+"F6.wireOp",EDGE,"E185.MirrorCS"),subQ0])],"isStart":false}),makeQuery(id+"F7.opExtrude","CAP_FACE",FACE,{"disambiguationData":[OSD([sQuery(id+"F6.wireOp",EDGE,"E119.MirrorCS"),sQuery(id+"F6.wireOp",EDGE,"E112.MirrorCS"),sQuery(id+"F6.wireOp",EDGE,"E111.MirrorCS"),subQ0])],"isStart":false}),makeQuery(id+"F7.opExtrude","CAP_FACE",FACE,{"disambiguationData":[OSD([sQuery(id+"F6.wireOp",EDGE,"E138.MirrorCS"),sQuery(id+"F6.wireOp",EDGE,"E187.MirrorCS"),sQuery(id+"F6.wireOp",EDGE,"E134.MirrorCS"),subQ0])],"isStart":false}),makeQuery(id+"F7.opExtrude","CAP_FACE",FACE,{"disambiguationData":[OSD([sQuery(id+"F6.wireOp",EDGE,"E118.MirrorCS"),sQuery(id+"F6.wireOp",EDGE,"E140.MirrorCS"),sQuery(id+"F6.wireOp",EDGE,"E115.MirrorCS"),subQ0])],"isStart":false}),makeQuery(id+"F7.opExtrude","CAP_FACE",FACE,{"disambiguationData":[OSD([sQuery(id+"F6.wireOp",EDGE,"E160.MirrorCS"),sQuery(id+"F6.wireOp",EDGE,"E198.MirrorCS"),sQuery(id+"F6.wireOp",EDGE,"E148.MirrorCS"),subQ0])],"isStart":false}),makeQuery(id+"F7.opExtrude","CAP_FACE",FACE,{"disambiguationData":[OSD([sQuery(id+"F6.wireOp",EDGE,"E203.MirrorCS"),sQuery(id+"F6.wireOp",EDGE,"E166.MirrorCS"),sQuery(id+"F6.wireOp",EDGE,"E165.MirrorCS"),subQ0])],"isStart":false}),makeQuery(id+"F7.opExtrude","CAP_FACE",FACE,{"disambiguationData":[OSD([sQuery(id+"F6.wireOp",EDGE,"E200.MirrorCS"),sQuery(id+"F6.wireOp",EDGE,"E156.MirrorCS"),sQuery(id+"F6.wireOp",EDGE,"E158.MirrorCS"),subQ0])],"isStart":false}),makeQuery(id+"F7.opExtrude","CAP_FACE",FACE,{"disambiguationData":[OSD([sQuery(id+"F6.wireOp",EDGE,"E161.MirrorCS"),sQuery(id+"F6.wireOp",EDGE,"E167.MirrorCS"),sQuery(id+"F6.wireOp",EDGE,"E202.MirrorCS"),subQ0])],"isStart":false}),makeQuery(id+"F7.opExtrude","CAP_FACE",FACE,{"disambiguationData":[OSD([sQuery(id+"F6.wireOp",EDGE,"E141.MirrorCS"),sQuery(id+"F6.wireOp",EDGE,"E157.MirrorCS"),sQuery(id+"F6.wireOp",EDGE,"E199.MirrorCS"),subQ0])],"isStart":false}),makeQuery(id+"F7.opExtrude","CAP_FACE",FACE,{"disambiguationData":[OSD([sQuery(id+"F6.wireOp",EDGE,"E204.MirrorCS"),sQuery(id+"F6.wireOp",EDGE,"E164.MirrorCS"),sQuery(id+"F6.wireOp",EDGE,"E163.MirrorCS"),subQ0])],"isStart":false}),makeQuery(id+"F7.opExtrude","CAP_FACE",FACE,{"disambiguationData":[OSD([sQuery(id+"F6.wireOp",EDGE,"E168.MirrorCS"),sQuery(id+"F6.wireOp",EDGE,"E162.MirrorCS"),sQuery(id+"F6.wireOp",EDGE,"E201.MirrorCS"),subQ0])],"isStart":false}),makeQuery(id+"F7.opExtrude","CAP_FACE",FACE,{"disambiguationData":[OSD([sQuery(id+"F6.wireOp",EDGE,"E207.MirrorCS"),sQuery(id+"F6.wireOp",EDGE,"E170.MirrorCS"),sQuery(id+"F6.wireOp",EDGE,"E174.MirrorCS"),subQ0])],"isStart":false}),makeQuery(id+"F7.opExtrude","CAP_FACE",FACE,{"disambiguationData":[OSD([sQuery(id+"F6.wireOp",EDGE,"E192.MirrorCS"),sQuery(id+"F6.wireOp",EDGE,"E178.MirrorCS"),sQuery(id+"F6.wireOp",EDGE,"E212.MirrorCS"),subQ0])],"isStart":false}),makeQuery(id+"F7.opExtrude","CAP_FACE",FACE,{"disambiguationData":[OSD([sQuery(id+"F6.wireOp",EDGE,"E171.MirrorCS"),sQuery(id+"F6.wireOp",EDGE,"E205.MirrorCS"),sQuery(id+"F6.wireOp",EDGE,"E172.MirrorCS"),subQ0])],"isStart":false}),makeQuery(id+"F7.opExtrude","CAP_FACE",FACE,{"disambiguationData":[OSD([sQuery(id+"F6.wireOp",EDGE,"E206.MirrorCS"),sQuery(id+"F6.wireOp",EDGE,"E169.MirrorCS"),sQuery(id+"F6.wireOp",EDGE,"E188.MirrorCS"),subQ0])],"isStart":false}),makeQuery(id+"F7.opExtrude","CAP_FACE",FACE,{"disambiguationData":[OSD([sQuery(id+"F6.wireOp",EDGE,"E195.MirrorCS"),sQuery(id+"F6.wireOp",EDGE,"E210.MirrorCS"),sQuery(id+"F6.wireOp",EDGE,"E211.MirrorCS"),subQ0])],"isStart":false}),makeQuery(id+"F7.opExtrude","CAP_FACE",FACE,{"disambiguationData":[OSD([sQuery(id+"F6.wireOp",EDGE,"E209.MirrorCS"),sQuery(id+"F6.wireOp",EDGE,"E173.MirrorCS"),sQuery(id+"F6.wireOp",EDGE,"E175.MirrorCS"),subQ0])],"isStart":false})]});Q0=makeQuery(id+"F9.boolean.opBoolean","MERGE",FACE,{"derivedFrom":[subQ3,makeQuery(id+"F9.opPattern","COPY",FACE,{"derivedFrom":subQ3,"instanceName":"1"})]});}
            var sketch = newSketch(context, id + "F10", { "sketchPlane" : qUnion([Q0])});
            skLineSegment(sketch, "E214.bottom", {"start": v(55.56, -225.05) * mm, "end": v(-71.36, -225.05) * mm});
            skLineSegment(sketch, "E214.top", {"start": v(55.56, -260.03) * mm, "end": v(-71.36, -260.03) * mm});
            skLineSegment(sketch, "E214.left", {"start": v(55.56, -225.05) * mm, "end": v(55.56, -260.03) * mm});
            skLineSegment(sketch, "E214.right", {"start": v(-71.36, -225.05) * mm, "end": v(-71.36, -260.03) * mm});
            skSolve(sketch);
        }
        {
            var Q0;
            {var subQ1=sQuery(id+"F6.wireOp",EDGE,"E65.top");var subQ2=makeQuery(id+"F9.opPattern","COPY",EDGE,{"derivedFrom":makeQuery(id+"F7.opExtrude","CAP_EDGE",EDGE,{"disambiguationData":[OSD([subQ1])],"isStart":false}),"instanceName":"1"});Q0=makeQuery(id+"F10.imprint","IMPRINT",FACE,{"disambiguationData":[TD([[makeQuery(id+"F10.imprint","IMPRINT",EDGE,{"derivedFrom":subQ2}),1.0]])]});}
            var Q1;
            {var subQ1=sQuery(id+"F6.wireOp",EDGE,"E67.top");var subQ2=makeQuery(id+"F9.opPattern","COPY",EDGE,{"derivedFrom":makeQuery(id+"F7.opExtrude","CAP_EDGE",EDGE,{"disambiguationData":[OSD([subQ1])],"isStart":false}),"instanceName":"1"});Q1=makeQuery(id+"F10.imprint","IMPRINT",FACE,{"disambiguationData":[TD([[makeQuery(id+"F10.imprint","IMPRINT",EDGE,{"derivedFrom":subQ2}),1.0]])]});}
            var Q2;
            {var subQ1=sQuery(id+"F6.wireOp",EDGE,"E69.top");var subQ2=makeQuery(id+"F9.opPattern","COPY",EDGE,{"derivedFrom":makeQuery(id+"F7.opExtrude","CAP_EDGE",EDGE,{"disambiguationData":[OSD([subQ1])],"isStart":false}),"instanceName":"1"});Q2=makeQuery(id+"F10.imprint","IMPRINT",FACE,{"disambiguationData":[TD([[makeQuery(id+"F10.imprint","IMPRINT",EDGE,{"derivedFrom":subQ2}),1.0]])]});}
            var Q3;
            {var subQ4=sQuery(id+"F6.wireOp",EDGE,"E65.bottom");var subQ11=makeQuery(id+"F9.opPattern","COPY",EDGE,{"derivedFrom":makeQuery(id+"F7.opExtrude","CAP_EDGE",EDGE,{"disambiguationData":[OSD([subQ4])],"isStart":false}),"instanceName":"1"});Q3=makeQuery(id+"F10.imprint","IMPRINT",FACE,{"disambiguationData":[TD([[makeQuery(id+"F10.imprint","IMPRINT",EDGE,{"derivedFrom":subQ11}),-1.0]])]});}
            var Q4;
            {var subQ140=sQuery(id+"F10.wireOp",EDGE,"E214.top");Q4=makeQuery(id+"F10.imprint","IMPRINT",FACE,{"disambiguationData":[TD([[makeQuery(id+"F10.imprint","IMPRINT",EDGE,{"derivedFrom":subQ140}),-1.0]])]});}
            var Q5;
            {var subQ2=sQuery(id+"F0.wireOp",EDGE,"E0.top");var subQ6=sQuery(id+"F0.wireOp",EDGE,"E1");var subQ7=sQuery(id+"F0.wireOp",EDGE,"E0.left");var subQ8=makeQuery(id+"F1.opExtrude","CAP_VERTEX",VERTEX,{"disambiguationData":[OSD([subQ2,subQ7,subQ6])],"isStart":true});var subQ12=makeQuery(id+"F9.opPattern","COPY",EDGE,{"derivedFrom":makeQuery(id+"F5.boolean.opBoolean","MERGE",EDGE,{"derivedFrom":[makeQuery(id+"F3.boolean.opBoolean","COPY",EDGE,{"derivedFrom":makeQuery(id+"F3.opExtrude","CAP_EDGE",EDGE,{"disambiguationData":[OSD([subQ2]),TDD([makeQuery(id+"F1.opExtrude","CAP_EDGE",EDGE,{"disambiguationData":[OSD([subQ2])],"isStart":true})])],"isStart":false})}),makeQuery(id+"F5.opExtrude","SWEPT_EDGE",EDGE,{"disambiguationData":[OSD([subQ2,subQ7,subQ6]),TDD([makeQuery(id+"F3.boolean.opBoolean","COPY",VERTEX,{"derivedFrom":makeQuery(id+"F3.opExtrude","CAP_VERTEX",VERTEX,{"disambiguationData":[OSD([subQ2,subQ7,subQ6]),TDD([subQ8])],"isStart":false})})])]})]}),"instanceName":"1"});Q5=makeQuery(id+"F10.imprint","IMPRINT",FACE,{"disambiguationData":[TD([[makeQuery(id+"F10.imprint","IMPRINT",EDGE,{"derivedFrom":subQ12}),1.0]])]});}
            var Q6;
            {var subQ5=sQuery(id+"F0.wireOp",EDGE,"E0.left");var subQ6=sQuery(id+"F0.wireOp",EDGE,"E0.top");var subQ134=sQuery(id+"F0.wireOp",EDGE,"E1");var subQ135=makeQuery(id+"F1.opExtrude","CAP_VERTEX",VERTEX,{"disambiguationData":[OSD([subQ6,subQ5,subQ134])],"isStart":true});var subQ145=makeQuery(id+"F9.opPattern","COPY",EDGE,{"derivedFrom":makeQuery(id+"F5.boolean.opBoolean","MERGE",EDGE,{"derivedFrom":[makeQuery(id+"F3.boolean.opBoolean","COPY",EDGE,{"derivedFrom":makeQuery(id+"F3.opExtrude","CAP_EDGE",EDGE,{"disambiguationData":[OSD([subQ6]),TDD([makeQuery(id+"F1.opExtrude","CAP_EDGE",EDGE,{"disambiguationData":[OSD([subQ6])],"isStart":true})])],"isStart":false})}),makeQuery(id+"F5.opExtrude","SWEPT_EDGE",EDGE,{"disambiguationData":[OSD([subQ6,subQ5,subQ134]),TDD([makeQuery(id+"F3.boolean.opBoolean","COPY",VERTEX,{"derivedFrom":makeQuery(id+"F3.opExtrude","CAP_VERTEX",VERTEX,{"disambiguationData":[OSD([subQ6,subQ5,subQ134]),TDD([subQ135])],"isStart":false})})])]})]}),"instanceName":"1"});Q6=makeQuery(id+"F10.imprint","IMPRINT",FACE,{"disambiguationData":[TD([[makeQuery(id+"F10.imprint","IMPRINT",EDGE,{"derivedFrom":subQ145}),-1.0]])]});}
            extrude(context, id + "F11", {"entities" : qUnion([Q0, Q1, Q2, Q3, Q4, Q5, Q6]), "operationType" : NewBodyOperationType.REMOVE, "endBound" : BoundingType.THROUGH_ALL, "oppositeDirection" : true, "depth" : 25 * mm, "offsetDistance" : 25 * mm});
        }
    });
